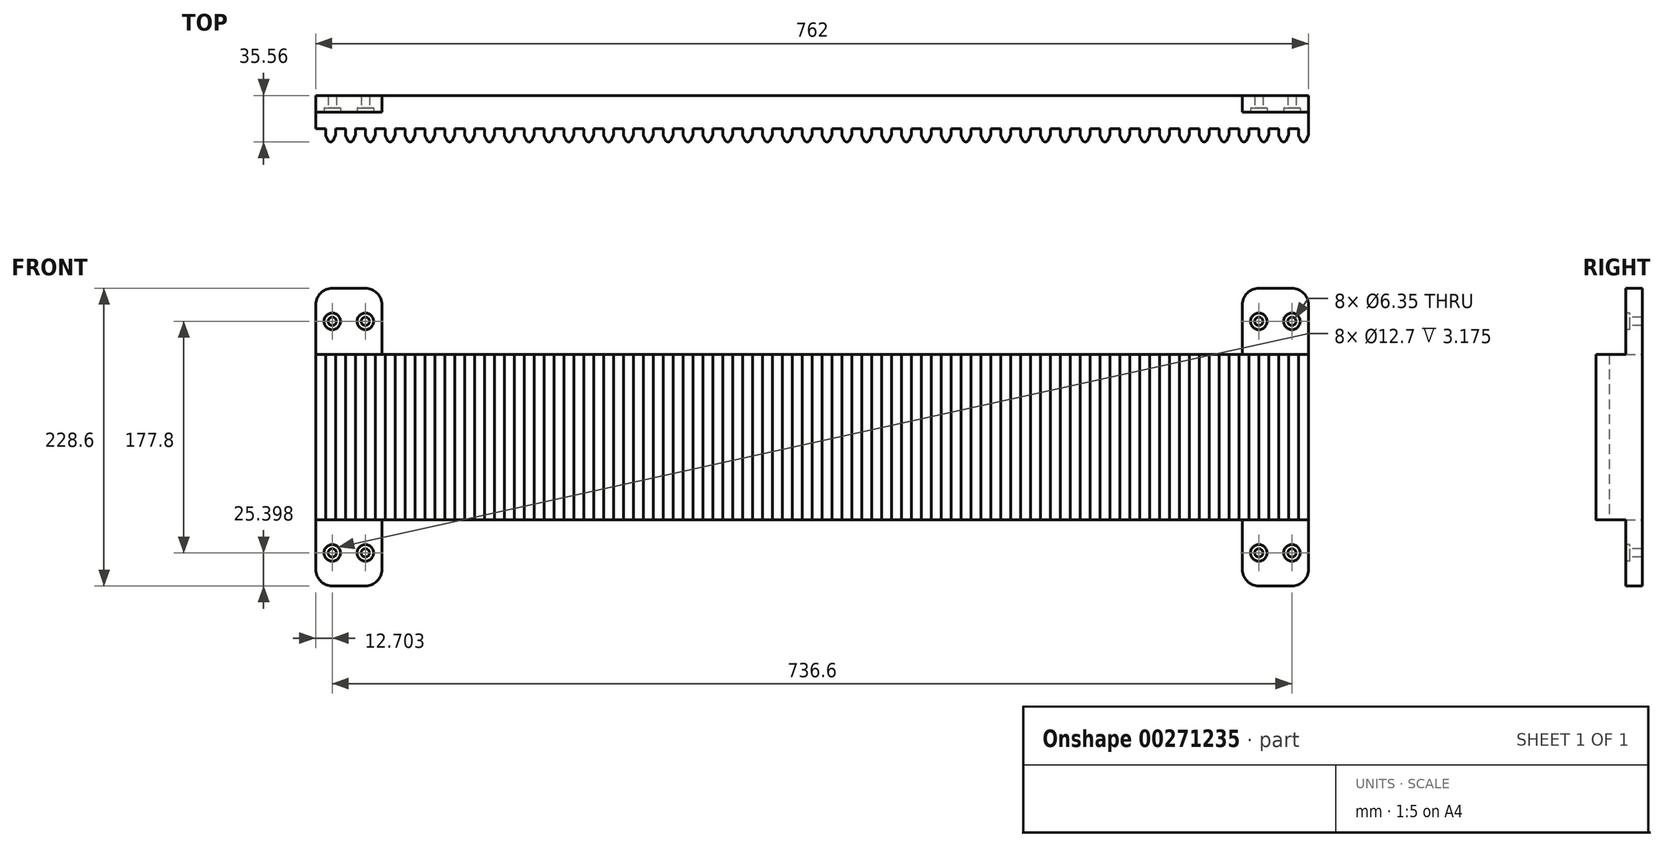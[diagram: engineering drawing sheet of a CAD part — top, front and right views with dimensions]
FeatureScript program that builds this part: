
annotation { "Feature Type Name" : "Feature", "Feature Type Description" : "" }
export const myFeature = defineFeature(function(context is Context, id is Id, definition is map)
    precondition{}
    {
        {
            var Q0;
            Q0=qCreatedBy(makeId("Front.planeOp"),FACE);
            var sketch = newSketch(context, id + "F0", { "sketchPlane" : qUnion([Q0])});
            skLineSegment(sketch, "E0", {"start": v(-383.67, -271.66) * mm, "end": v(378.33, -271.66) * mm});
            skLineSegment(sketch, "E1", {"start": v(378.33, -271.66) * mm, "end": v(378.33, -144.66) * mm});
            skLineSegment(sketch, "E2", {"start": v(378.33, -144.66) * mm, "end": v(-383.67, -144.66) * mm});
            skLineSegment(sketch, "E3", {"start": v(-383.67, -144.66) * mm, "end": v(-383.67, -271.66) * mm});
            skSolve(sketch);
        }
        {
            var Q0;
            Q0=makeQuery(id+"F0.imprint","IMPRINT",FACE,{"disambiguationData":[TD([[makeQuery(id+"F0.imprint","IMPRINT",EDGE,{"derivedFrom":sQuery(id+"F0.wireOp",EDGE,"E0")}),1.0]])]});
            extrude(context, id + "F1", {"entities" : qUnion([Q0]), "depth" : 25.4 * mm});
        }
        {
            var Q0;
            Q0=makeQuery(id+"F1.opExtrude","SWEPT_FACE",FACE,{"disambiguationData":[OSD([sQuery(id+"F0.wireOp",EDGE,"E0")])]});
            var sketch = newSketch(context, id + "F2", { "sketchPlane" : qUnion([Q0])});
            skLineSegment(sketch, "E4", {"start": v(-383.67, 25.4) * mm, "end": v(-376.05, 25.4) * mm});
            skLineSegment(sketch, "E5", {"start": v(-376.05, 25.4) * mm, "end": v(-376.05, 30.48) * mm});
            skLineSegment(sketch, "E6", {"start": v(-375.9, 30.8) * mm, "end": v(-374.1, 34.64) * mm});
            skLineSegment(sketch, "E7", {"start": v(-372.67, 35.56) * mm, "end": v(-371.8, 35.56) * mm});
            skLineSegment(sketch, "E8", {"start": v(-370.37, 34.64) * mm, "end": v(-368.58, 30.8) * mm});
            skLineSegment(sketch, "E9", {"start": v(-368.43, 30.13) * mm, "end": v(-368.43, 25.4) * mm});
            skLineSegment(sketch, "E10", {"start": v(-376.05, 30.13) * mm, "end": v(-376.05, 25.4) * mm});
            skPoint(sketch, "E11.visualSharp", {"position": v(-376.05, 30.48) * mm});
            skArc(sketch, "E11.filletArc", {"start": v(-375.9, 30.8) * mm, "mid": v(-376, 30.47) * mm, "end": v(-376.05, 30.13) * mm});
            skPoint(sketch, "E12.visualSharp", {"position": v(-368.43, 30.48) * mm});
            skArc(sketch, "E12.filletArc", {"start": v(-368.43, 30.13) * mm, "mid": v(-368.46, 30.47) * mm, "end": v(-368.58, 30.8) * mm});
            skPoint(sketch, "E13.visualSharp", {"position": v(-373.68, 35.56) * mm});
            skArc(sketch, "E13.filletArc", {"start": v(-372.67, 35.56) * mm, "mid": v(-373.52, 35.31) * mm, "end": v(-374.1, 34.64) * mm});
            skPoint(sketch, "E14.visualSharp", {"position": v(-370.8, 35.56) * mm});
            skArc(sketch, "E14.filletArc", {"start": v(-370.37, 34.64) * mm, "mid": v(-370.95, 35.31) * mm, "end": v(-371.8, 35.56) * mm});
            skLineSegment(sketch, "E15.1.0.0", {"start": v(-368.43, 25.4) * mm, "end": v(-360.8, 25.4) * mm});
            skLineSegment(sketch, "E15.1.0.1", {"start": v(-360.8, 30.13) * mm, "end": v(-360.8, 25.4) * mm});
            skArc(sketch, "E15.1.0.2", {"start": v(-360.66, 30.8) * mm, "mid": v(-360.77, 30.47) * mm, "end": v(-360.8, 30.13) * mm});
            skLineSegment(sketch, "E15.1.0.3", {"start": v(-360.66, 30.8) * mm, "end": v(-358.87, 34.64) * mm});
            skArc(sketch, "E15.1.0.4", {"start": v(-357.43, 35.56) * mm, "mid": v(-358.28, 35.31) * mm, "end": v(-358.87, 34.64) * mm});
            skLineSegment(sketch, "E15.1.0.5", {"start": v(-357.43, 35.56) * mm, "end": v(-356.57, 35.56) * mm});
            skArc(sketch, "E15.1.0.6", {"start": v(-355.13, 34.64) * mm, "mid": v(-355.71, 35.31) * mm, "end": v(-356.57, 35.56) * mm});
            skLineSegment(sketch, "E15.1.0.7", {"start": v(-355.13, 34.64) * mm, "end": v(-353.34, 30.8) * mm});
            skArc(sketch, "E15.1.0.8", {"start": v(-353.19, 30.13) * mm, "mid": v(-353.22, 30.47) * mm, "end": v(-353.34, 30.8) * mm});
            skLineSegment(sketch, "E15.1.0.9", {"start": v(-353.19, 30.13) * mm, "end": v(-353.19, 25.4) * mm});
            skLineSegment(sketch, "E15.2.0.0", {"start": v(-353.19, 25.4) * mm, "end": v(-345.57, 25.4) * mm});
            skLineSegment(sketch, "E15.2.0.1", {"start": v(-345.57, 30.13) * mm, "end": v(-345.57, 25.4) * mm});
            skArc(sketch, "E15.2.0.2", {"start": v(-345.42, 30.8) * mm, "mid": v(-345.53, 30.47) * mm, "end": v(-345.57, 30.13) * mm});
            skLineSegment(sketch, "E15.2.0.3", {"start": v(-345.42, 30.8) * mm, "end": v(-343.63, 34.64) * mm});
            skArc(sketch, "E15.2.0.4", {"start": v(-342.19, 35.56) * mm, "mid": v(-343.04, 35.31) * mm, "end": v(-343.63, 34.64) * mm});
            skLineSegment(sketch, "E15.2.0.5", {"start": v(-342.19, 35.56) * mm, "end": v(-341.33, 35.56) * mm});
            skArc(sketch, "E15.2.0.6", {"start": v(-339.89, 34.64) * mm, "mid": v(-340.47, 35.31) * mm, "end": v(-341.33, 35.56) * mm});
            skLineSegment(sketch, "E15.2.0.7", {"start": v(-339.89, 34.64) * mm, "end": v(-338.1, 30.8) * mm});
            skArc(sketch, "E15.2.0.8", {"start": v(-337.95, 30.13) * mm, "mid": v(-337.98, 30.47) * mm, "end": v(-338.1, 30.8) * mm});
            skLineSegment(sketch, "E15.2.0.9", {"start": v(-337.95, 30.13) * mm, "end": v(-337.95, 25.4) * mm});
            skLineSegment(sketch, "E15.3.0.0", {"start": v(-337.95, 25.4) * mm, "end": v(-330.33, 25.4) * mm});
            skLineSegment(sketch, "E15.3.0.1", {"start": v(-330.33, 30.13) * mm, "end": v(-330.33, 25.4) * mm});
            skArc(sketch, "E15.3.0.2", {"start": v(-330.18, 30.8) * mm, "mid": v(-330.29, 30.47) * mm, "end": v(-330.33, 30.13) * mm});
            skLineSegment(sketch, "E15.3.0.3", {"start": v(-330.18, 30.8) * mm, "end": v(-328.39, 34.64) * mm});
            skArc(sketch, "E15.3.0.4", {"start": v(-326.95, 35.56) * mm, "mid": v(-327.8, 35.31) * mm, "end": v(-328.39, 34.64) * mm});
            skLineSegment(sketch, "E15.3.0.5", {"start": v(-326.95, 35.56) * mm, "end": v(-326.09, 35.56) * mm});
            skArc(sketch, "E15.3.0.6", {"start": v(-324.65, 34.64) * mm, "mid": v(-325.23, 35.31) * mm, "end": v(-326.09, 35.56) * mm});
            skLineSegment(sketch, "E15.3.0.7", {"start": v(-324.65, 34.64) * mm, "end": v(-322.86, 30.8) * mm});
            skArc(sketch, "E15.3.0.8", {"start": v(-322.7, 30.13) * mm, "mid": v(-322.74, 30.47) * mm, "end": v(-322.86, 30.8) * mm});
            skLineSegment(sketch, "E15.3.0.9", {"start": v(-322.7, 30.13) * mm, "end": v(-322.7, 25.4) * mm});
            skLineSegment(sketch, "E15.4.0.0", {"start": v(-322.7, 25.4) * mm, "end": v(-315.09, 25.4) * mm});
            skLineSegment(sketch, "E15.4.0.1", {"start": v(-315.09, 30.13) * mm, "end": v(-315.09, 25.4) * mm});
            skArc(sketch, "E15.4.0.2", {"start": v(-314.94, 30.8) * mm, "mid": v(-315.05, 30.47) * mm, "end": v(-315.09, 30.13) * mm});
            skLineSegment(sketch, "E15.4.0.3", {"start": v(-314.94, 30.8) * mm, "end": v(-313.15, 34.64) * mm});
            skArc(sketch, "E15.4.0.4", {"start": v(-311.7, 35.56) * mm, "mid": v(-312.56, 35.31) * mm, "end": v(-313.15, 34.64) * mm});
            skLineSegment(sketch, "E15.4.0.5", {"start": v(-311.7, 35.56) * mm, "end": v(-310.85, 35.56) * mm});
            skArc(sketch, "E15.4.0.6", {"start": v(-309.4, 34.64) * mm, "mid": v(-310, 35.31) * mm, "end": v(-310.85, 35.56) * mm});
            skLineSegment(sketch, "E15.4.0.7", {"start": v(-309.4, 34.64) * mm, "end": v(-307.62, 30.8) * mm});
            skArc(sketch, "E15.4.0.8", {"start": v(-307.47, 30.13) * mm, "mid": v(-307.5, 30.47) * mm, "end": v(-307.62, 30.8) * mm});
            skLineSegment(sketch, "E15.4.0.9", {"start": v(-307.47, 30.13) * mm, "end": v(-307.47, 25.4) * mm});
            skLineSegment(sketch, "E15.5.0.0", {"start": v(-307.47, 25.4) * mm, "end": v(-299.85, 25.4) * mm});
            skLineSegment(sketch, "E15.5.0.1", {"start": v(-299.85, 30.13) * mm, "end": v(-299.85, 25.4) * mm});
            skArc(sketch, "E15.5.0.2", {"start": v(-299.7, 30.8) * mm, "mid": v(-299.8, 30.47) * mm, "end": v(-299.85, 30.13) * mm});
            skLineSegment(sketch, "E15.5.0.3", {"start": v(-299.7, 30.8) * mm, "end": v(-297.9, 34.64) * mm});
            skArc(sketch, "E15.5.0.4", {"start": v(-296.47, 35.56) * mm, "mid": v(-297.32, 35.31) * mm, "end": v(-297.9, 34.64) * mm});
            skLineSegment(sketch, "E15.5.0.5", {"start": v(-296.47, 35.56) * mm, "end": v(-295.6, 35.56) * mm});
            skArc(sketch, "E15.5.0.6", {"start": v(-294.17, 34.64) * mm, "mid": v(-294.75, 35.31) * mm, "end": v(-295.6, 35.56) * mm});
            skLineSegment(sketch, "E15.5.0.7", {"start": v(-294.17, 34.64) * mm, "end": v(-292.38, 30.8) * mm});
            skArc(sketch, "E15.5.0.8", {"start": v(-292.23, 30.13) * mm, "mid": v(-292.26, 30.47) * mm, "end": v(-292.38, 30.8) * mm});
            skLineSegment(sketch, "E15.5.0.9", {"start": v(-292.23, 30.13) * mm, "end": v(-292.23, 25.4) * mm});
            skLineSegment(sketch, "E15.6.0.0", {"start": v(-292.23, 25.4) * mm, "end": v(-284.6, 25.4) * mm});
            skLineSegment(sketch, "E15.6.0.1", {"start": v(-284.6, 30.13) * mm, "end": v(-284.6, 25.4) * mm});
            skArc(sketch, "E15.6.0.2", {"start": v(-284.46, 30.8) * mm, "mid": v(-284.57, 30.47) * mm, "end": v(-284.6, 30.13) * mm});
            skLineSegment(sketch, "E15.6.0.3", {"start": v(-284.46, 30.8) * mm, "end": v(-282.67, 34.64) * mm});
            skArc(sketch, "E15.6.0.4", {"start": v(-281.23, 35.56) * mm, "mid": v(-282.08, 35.31) * mm, "end": v(-282.67, 34.64) * mm});
            skLineSegment(sketch, "E15.6.0.5", {"start": v(-281.23, 35.56) * mm, "end": v(-280.37, 35.56) * mm});
            skArc(sketch, "E15.6.0.6", {"start": v(-278.93, 34.64) * mm, "mid": v(-279.51, 35.31) * mm, "end": v(-280.37, 35.56) * mm});
            skLineSegment(sketch, "E15.6.0.7", {"start": v(-278.93, 34.64) * mm, "end": v(-277.14, 30.8) * mm});
            skArc(sketch, "E15.6.0.8", {"start": v(-276.99, 30.13) * mm, "mid": v(-277.02, 30.47) * mm, "end": v(-277.14, 30.8) * mm});
            skLineSegment(sketch, "E15.6.0.9", {"start": v(-276.99, 30.13) * mm, "end": v(-276.99, 25.4) * mm});
            skLineSegment(sketch, "E15.7.0.0", {"start": v(-276.99, 25.4) * mm, "end": v(-269.37, 25.4) * mm});
            skLineSegment(sketch, "E15.7.0.1", {"start": v(-269.37, 30.13) * mm, "end": v(-269.37, 25.4) * mm});
            skArc(sketch, "E15.7.0.2", {"start": v(-269.22, 30.8) * mm, "mid": v(-269.33, 30.47) * mm, "end": v(-269.37, 30.13) * mm});
            skLineSegment(sketch, "E15.7.0.3", {"start": v(-269.22, 30.8) * mm, "end": v(-267.43, 34.64) * mm});
            skArc(sketch, "E15.7.0.4", {"start": v(-265.99, 35.56) * mm, "mid": v(-266.84, 35.31) * mm, "end": v(-267.43, 34.64) * mm});
            skLineSegment(sketch, "E15.7.0.5", {"start": v(-265.99, 35.56) * mm, "end": v(-265.13, 35.56) * mm});
            skArc(sketch, "E15.7.0.6", {"start": v(-263.69, 34.64) * mm, "mid": v(-264.27, 35.31) * mm, "end": v(-265.13, 35.56) * mm});
            skLineSegment(sketch, "E15.7.0.7", {"start": v(-263.69, 34.64) * mm, "end": v(-261.9, 30.8) * mm});
            skArc(sketch, "E15.7.0.8", {"start": v(-261.75, 30.13) * mm, "mid": v(-261.78, 30.47) * mm, "end": v(-261.9, 30.8) * mm});
            skLineSegment(sketch, "E15.7.0.9", {"start": v(-261.75, 30.13) * mm, "end": v(-261.75, 25.4) * mm});
            skLineSegment(sketch, "E15.8.0.0", {"start": v(-261.75, 25.4) * mm, "end": v(-254.13, 25.4) * mm});
            skLineSegment(sketch, "E15.8.0.1", {"start": v(-254.13, 30.13) * mm, "end": v(-254.13, 25.4) * mm});
            skArc(sketch, "E15.8.0.2", {"start": v(-253.98, 30.8) * mm, "mid": v(-254.09, 30.47) * mm, "end": v(-254.13, 30.13) * mm});
            skLineSegment(sketch, "E15.8.0.3", {"start": v(-253.98, 30.8) * mm, "end": v(-252.19, 34.64) * mm});
            skArc(sketch, "E15.8.0.4", {"start": v(-250.75, 35.56) * mm, "mid": v(-251.6, 35.31) * mm, "end": v(-252.19, 34.64) * mm});
            skLineSegment(sketch, "E15.8.0.5", {"start": v(-250.75, 35.56) * mm, "end": v(-249.89, 35.56) * mm});
            skArc(sketch, "E15.8.0.6", {"start": v(-248.45, 34.64) * mm, "mid": v(-249.03, 35.31) * mm, "end": v(-249.89, 35.56) * mm});
            skLineSegment(sketch, "E15.8.0.7", {"start": v(-248.45, 34.64) * mm, "end": v(-246.66, 30.8) * mm});
            skArc(sketch, "E15.8.0.8", {"start": v(-246.5, 30.13) * mm, "mid": v(-246.54, 30.47) * mm, "end": v(-246.66, 30.8) * mm});
            skLineSegment(sketch, "E15.8.0.9", {"start": v(-246.5, 30.13) * mm, "end": v(-246.5, 25.4) * mm});
            skLineSegment(sketch, "E15.9.0.0", {"start": v(-246.5, 25.4) * mm, "end": v(-238.89, 25.4) * mm});
            skLineSegment(sketch, "E15.9.0.1", {"start": v(-238.89, 30.13) * mm, "end": v(-238.89, 25.4) * mm});
            skArc(sketch, "E15.9.0.2", {"start": v(-238.74, 30.8) * mm, "mid": v(-238.85, 30.47) * mm, "end": v(-238.89, 30.13) * mm});
            skLineSegment(sketch, "E15.9.0.3", {"start": v(-238.74, 30.8) * mm, "end": v(-236.95, 34.64) * mm});
            skArc(sketch, "E15.9.0.4", {"start": v(-235.5, 35.56) * mm, "mid": v(-236.36, 35.31) * mm, "end": v(-236.95, 34.64) * mm});
            skLineSegment(sketch, "E15.9.0.5", {"start": v(-235.5, 35.56) * mm, "end": v(-234.65, 35.56) * mm});
            skArc(sketch, "E15.9.0.6", {"start": v(-233.2, 34.64) * mm, "mid": v(-233.8, 35.31) * mm, "end": v(-234.65, 35.56) * mm});
            skLineSegment(sketch, "E15.9.0.7", {"start": v(-233.2, 34.64) * mm, "end": v(-231.42, 30.8) * mm});
            skArc(sketch, "E15.9.0.8", {"start": v(-231.27, 30.13) * mm, "mid": v(-231.3, 30.47) * mm, "end": v(-231.42, 30.8) * mm});
            skLineSegment(sketch, "E15.9.0.9", {"start": v(-231.27, 30.13) * mm, "end": v(-231.27, 25.4) * mm});
            skLineSegment(sketch, "E15.10.0.0", {"start": v(-231.27, 25.4) * mm, "end": v(-223.65, 25.4) * mm});
            skLineSegment(sketch, "E15.10.0.1", {"start": v(-223.65, 30.13) * mm, "end": v(-223.65, 25.4) * mm});
            skArc(sketch, "E15.10.0.2", {"start": v(-223.5, 30.8) * mm, "mid": v(-223.6, 30.47) * mm, "end": v(-223.65, 30.13) * mm});
            skLineSegment(sketch, "E15.10.0.3", {"start": v(-223.5, 30.8) * mm, "end": v(-221.7, 34.64) * mm});
            skArc(sketch, "E15.10.0.4", {"start": v(-220.27, 35.56) * mm, "mid": v(-221.12, 35.31) * mm, "end": v(-221.7, 34.64) * mm});
            skLineSegment(sketch, "E15.10.0.5", {"start": v(-220.27, 35.56) * mm, "end": v(-219.4, 35.56) * mm});
            skArc(sketch, "E15.10.0.6", {"start": v(-217.97, 34.64) * mm, "mid": v(-218.55, 35.31) * mm, "end": v(-219.4, 35.56) * mm});
            skLineSegment(sketch, "E15.10.0.7", {"start": v(-217.97, 34.64) * mm, "end": v(-216.18, 30.8) * mm});
            skArc(sketch, "E15.10.0.8", {"start": v(-216.03, 30.13) * mm, "mid": v(-216.06, 30.47) * mm, "end": v(-216.18, 30.8) * mm});
            skLineSegment(sketch, "E15.10.0.9", {"start": v(-216.03, 30.13) * mm, "end": v(-216.03, 25.4) * mm});
            skLineSegment(sketch, "E15.11.0.0", {"start": v(-216.03, 25.4) * mm, "end": v(-208.4, 25.4) * mm});
            skLineSegment(sketch, "E15.11.0.1", {"start": v(-208.4, 30.13) * mm, "end": v(-208.4, 25.4) * mm});
            skArc(sketch, "E15.11.0.2", {"start": v(-208.26, 30.8) * mm, "mid": v(-208.37, 30.47) * mm, "end": v(-208.4, 30.13) * mm});
            skLineSegment(sketch, "E15.11.0.3", {"start": v(-208.26, 30.8) * mm, "end": v(-206.47, 34.64) * mm});
            skArc(sketch, "E15.11.0.4", {"start": v(-205.03, 35.56) * mm, "mid": v(-205.88, 35.31) * mm, "end": v(-206.47, 34.64) * mm});
            skLineSegment(sketch, "E15.11.0.5", {"start": v(-205.03, 35.56) * mm, "end": v(-204.17, 35.56) * mm});
            skArc(sketch, "E15.11.0.6", {"start": v(-202.73, 34.64) * mm, "mid": v(-203.31, 35.31) * mm, "end": v(-204.17, 35.56) * mm});
            skLineSegment(sketch, "E15.11.0.7", {"start": v(-202.73, 34.64) * mm, "end": v(-200.94, 30.8) * mm});
            skArc(sketch, "E15.11.0.8", {"start": v(-200.79, 30.13) * mm, "mid": v(-200.82, 30.47) * mm, "end": v(-200.94, 30.8) * mm});
            skLineSegment(sketch, "E15.11.0.9", {"start": v(-200.79, 30.13) * mm, "end": v(-200.79, 25.4) * mm});
            skLineSegment(sketch, "E15.12.0.0", {"start": v(-200.79, 25.4) * mm, "end": v(-193.17, 25.4) * mm});
            skLineSegment(sketch, "E15.12.0.1", {"start": v(-193.17, 30.13) * mm, "end": v(-193.17, 25.4) * mm});
            skArc(sketch, "E15.12.0.2", {"start": v(-193.02, 30.8) * mm, "mid": v(-193.13, 30.47) * mm, "end": v(-193.17, 30.13) * mm});
            skLineSegment(sketch, "E15.12.0.3", {"start": v(-193.02, 30.8) * mm, "end": v(-191.23, 34.64) * mm});
            skArc(sketch, "E15.12.0.4", {"start": v(-189.79, 35.56) * mm, "mid": v(-190.64, 35.31) * mm, "end": v(-191.23, 34.64) * mm});
            skLineSegment(sketch, "E15.12.0.5", {"start": v(-189.79, 35.56) * mm, "end": v(-188.93, 35.56) * mm});
            skArc(sketch, "E15.12.0.6", {"start": v(-187.49, 34.64) * mm, "mid": v(-188.07, 35.31) * mm, "end": v(-188.93, 35.56) * mm});
            skLineSegment(sketch, "E15.12.0.7", {"start": v(-187.49, 34.64) * mm, "end": v(-185.7, 30.8) * mm});
            skArc(sketch, "E15.12.0.8", {"start": v(-185.55, 30.13) * mm, "mid": v(-185.58, 30.47) * mm, "end": v(-185.7, 30.8) * mm});
            skLineSegment(sketch, "E15.12.0.9", {"start": v(-185.55, 30.13) * mm, "end": v(-185.55, 25.4) * mm});
            skLineSegment(sketch, "E15.13.0.0", {"start": v(-185.55, 25.4) * mm, "end": v(-177.93, 25.4) * mm});
            skLineSegment(sketch, "E15.13.0.1", {"start": v(-177.93, 30.13) * mm, "end": v(-177.93, 25.4) * mm});
            skArc(sketch, "E15.13.0.2", {"start": v(-177.78, 30.8) * mm, "mid": v(-177.89, 30.47) * mm, "end": v(-177.93, 30.13) * mm});
            skLineSegment(sketch, "E15.13.0.3", {"start": v(-177.78, 30.8) * mm, "end": v(-175.99, 34.64) * mm});
            skArc(sketch, "E15.13.0.4", {"start": v(-174.55, 35.56) * mm, "mid": v(-175.4, 35.31) * mm, "end": v(-175.99, 34.64) * mm});
            skLineSegment(sketch, "E15.13.0.5", {"start": v(-174.55, 35.56) * mm, "end": v(-173.69, 35.56) * mm});
            skArc(sketch, "E15.13.0.6", {"start": v(-172.25, 34.64) * mm, "mid": v(-172.83, 35.31) * mm, "end": v(-173.69, 35.56) * mm});
            skLineSegment(sketch, "E15.13.0.7", {"start": v(-172.25, 34.64) * mm, "end": v(-170.46, 30.8) * mm});
            skArc(sketch, "E15.13.0.8", {"start": v(-170.3, 30.13) * mm, "mid": v(-170.34, 30.47) * mm, "end": v(-170.46, 30.8) * mm});
            skLineSegment(sketch, "E15.13.0.9", {"start": v(-170.3, 30.13) * mm, "end": v(-170.3, 25.4) * mm});
            skLineSegment(sketch, "E15.14.0.0", {"start": v(-170.3, 25.4) * mm, "end": v(-162.69, 25.4) * mm});
            skLineSegment(sketch, "E15.14.0.1", {"start": v(-162.69, 30.13) * mm, "end": v(-162.69, 25.4) * mm});
            skArc(sketch, "E15.14.0.2", {"start": v(-162.54, 30.8) * mm, "mid": v(-162.65, 30.47) * mm, "end": v(-162.69, 30.13) * mm});
            skLineSegment(sketch, "E15.14.0.3", {"start": v(-162.54, 30.8) * mm, "end": v(-160.75, 34.64) * mm});
            skArc(sketch, "E15.14.0.4", {"start": v(-159.3, 35.56) * mm, "mid": v(-160.16, 35.31) * mm, "end": v(-160.75, 34.64) * mm});
            skLineSegment(sketch, "E15.14.0.5", {"start": v(-159.3, 35.56) * mm, "end": v(-158.45, 35.56) * mm});
            skArc(sketch, "E15.14.0.6", {"start": v(-157, 34.64) * mm, "mid": v(-157.6, 35.31) * mm, "end": v(-158.45, 35.56) * mm});
            skLineSegment(sketch, "E15.14.0.7", {"start": v(-157, 34.64) * mm, "end": v(-155.22, 30.8) * mm});
            skArc(sketch, "E15.14.0.8", {"start": v(-155.07, 30.13) * mm, "mid": v(-155.1, 30.47) * mm, "end": v(-155.22, 30.8) * mm});
            skLineSegment(sketch, "E15.14.0.9", {"start": v(-155.07, 30.13) * mm, "end": v(-155.07, 25.4) * mm});
            skLineSegment(sketch, "E15.15.0.0", {"start": v(-155.07, 25.4) * mm, "end": v(-147.45, 25.4) * mm});
            skLineSegment(sketch, "E15.15.0.1", {"start": v(-147.45, 30.13) * mm, "end": v(-147.45, 25.4) * mm});
            skArc(sketch, "E15.15.0.2", {"start": v(-147.3, 30.8) * mm, "mid": v(-147.4, 30.47) * mm, "end": v(-147.45, 30.13) * mm});
            skLineSegment(sketch, "E15.15.0.3", {"start": v(-147.3, 30.8) * mm, "end": v(-145.5, 34.64) * mm});
            skArc(sketch, "E15.15.0.4", {"start": v(-144.07, 35.56) * mm, "mid": v(-144.92, 35.31) * mm, "end": v(-145.5, 34.64) * mm});
            skLineSegment(sketch, "E15.15.0.5", {"start": v(-144.07, 35.56) * mm, "end": v(-143.2, 35.56) * mm});
            skArc(sketch, "E15.15.0.6", {"start": v(-141.77, 34.64) * mm, "mid": v(-142.35, 35.31) * mm, "end": v(-143.2, 35.56) * mm});
            skLineSegment(sketch, "E15.15.0.7", {"start": v(-141.77, 34.64) * mm, "end": v(-139.98, 30.8) * mm});
            skArc(sketch, "E15.15.0.8", {"start": v(-139.83, 30.13) * mm, "mid": v(-139.86, 30.47) * mm, "end": v(-139.98, 30.8) * mm});
            skLineSegment(sketch, "E15.15.0.9", {"start": v(-139.83, 30.13) * mm, "end": v(-139.83, 25.4) * mm});
            skLineSegment(sketch, "E15.16.0.0", {"start": v(-139.83, 25.4) * mm, "end": v(-132.2, 25.4) * mm});
            skLineSegment(sketch, "E15.16.0.1", {"start": v(-132.2, 30.13) * mm, "end": v(-132.2, 25.4) * mm});
            skArc(sketch, "E15.16.0.2", {"start": v(-132.06, 30.8) * mm, "mid": v(-132.17, 30.47) * mm, "end": v(-132.2, 30.13) * mm});
            skLineSegment(sketch, "E15.16.0.3", {"start": v(-132.06, 30.8) * mm, "end": v(-130.27, 34.64) * mm});
            skArc(sketch, "E15.16.0.4", {"start": v(-128.83, 35.56) * mm, "mid": v(-129.68, 35.31) * mm, "end": v(-130.27, 34.64) * mm});
            skLineSegment(sketch, "E15.16.0.5", {"start": v(-128.83, 35.56) * mm, "end": v(-127.97, 35.56) * mm});
            skArc(sketch, "E15.16.0.6", {"start": v(-126.53, 34.64) * mm, "mid": v(-127.11, 35.31) * mm, "end": v(-127.97, 35.56) * mm});
            skLineSegment(sketch, "E15.16.0.7", {"start": v(-126.53, 34.64) * mm, "end": v(-124.74, 30.8) * mm});
            skArc(sketch, "E15.16.0.8", {"start": v(-124.59, 30.13) * mm, "mid": v(-124.62, 30.47) * mm, "end": v(-124.74, 30.8) * mm});
            skLineSegment(sketch, "E15.16.0.9", {"start": v(-124.59, 30.13) * mm, "end": v(-124.59, 25.4) * mm});
            skLineSegment(sketch, "E15.17.0.0", {"start": v(-124.59, 25.4) * mm, "end": v(-116.97, 25.4) * mm});
            skLineSegment(sketch, "E15.17.0.1", {"start": v(-116.97, 30.13) * mm, "end": v(-116.97, 25.4) * mm});
            skArc(sketch, "E15.17.0.2", {"start": v(-116.82, 30.8) * mm, "mid": v(-116.93, 30.47) * mm, "end": v(-116.97, 30.13) * mm});
            skLineSegment(sketch, "E15.17.0.3", {"start": v(-116.82, 30.8) * mm, "end": v(-115.03, 34.64) * mm});
            skArc(sketch, "E15.17.0.4", {"start": v(-113.59, 35.56) * mm, "mid": v(-114.44, 35.31) * mm, "end": v(-115.03, 34.64) * mm});
            skLineSegment(sketch, "E15.17.0.5", {"start": v(-113.59, 35.56) * mm, "end": v(-112.73, 35.56) * mm});
            skArc(sketch, "E15.17.0.6", {"start": v(-111.29, 34.64) * mm, "mid": v(-111.87, 35.31) * mm, "end": v(-112.73, 35.56) * mm});
            skLineSegment(sketch, "E15.17.0.7", {"start": v(-111.29, 34.64) * mm, "end": v(-109.5, 30.8) * mm});
            skArc(sketch, "E15.17.0.8", {"start": v(-109.35, 30.13) * mm, "mid": v(-109.38, 30.47) * mm, "end": v(-109.5, 30.8) * mm});
            skLineSegment(sketch, "E15.17.0.9", {"start": v(-109.35, 30.13) * mm, "end": v(-109.35, 25.4) * mm});
            skLineSegment(sketch, "E15.18.0.0", {"start": v(-109.35, 25.4) * mm, "end": v(-101.73, 25.4) * mm});
            skLineSegment(sketch, "E15.18.0.1", {"start": v(-101.73, 30.13) * mm, "end": v(-101.73, 25.4) * mm});
            skArc(sketch, "E15.18.0.2", {"start": v(-101.58, 30.8) * mm, "mid": v(-101.69, 30.47) * mm, "end": v(-101.73, 30.13) * mm});
            skLineSegment(sketch, "E15.18.0.3", {"start": v(-101.58, 30.8) * mm, "end": v(-99.79, 34.64) * mm});
            skArc(sketch, "E15.18.0.4", {"start": v(-98.35, 35.56) * mm, "mid": v(-99.2, 35.31) * mm, "end": v(-99.79, 34.64) * mm});
            skLineSegment(sketch, "E15.18.0.5", {"start": v(-98.35, 35.56) * mm, "end": v(-97.49, 35.56) * mm});
            skArc(sketch, "E15.18.0.6", {"start": v(-96.05, 34.64) * mm, "mid": v(-96.63, 35.31) * mm, "end": v(-97.49, 35.56) * mm});
            skLineSegment(sketch, "E15.18.0.7", {"start": v(-96.05, 34.64) * mm, "end": v(-94.26, 30.8) * mm});
            skArc(sketch, "E15.18.0.8", {"start": v(-94.1, 30.13) * mm, "mid": v(-94.14, 30.47) * mm, "end": v(-94.26, 30.8) * mm});
            skLineSegment(sketch, "E15.18.0.9", {"start": v(-94.1, 30.13) * mm, "end": v(-94.1, 25.4) * mm});
            skLineSegment(sketch, "E15.19.0.0", {"start": v(-94.1, 25.4) * mm, "end": v(-86.49, 25.4) * mm});
            skLineSegment(sketch, "E15.19.0.1", {"start": v(-86.49, 30.13) * mm, "end": v(-86.49, 25.4) * mm});
            skArc(sketch, "E15.19.0.2", {"start": v(-86.34, 30.8) * mm, "mid": v(-86.45, 30.47) * mm, "end": v(-86.49, 30.13) * mm});
            skLineSegment(sketch, "E15.19.0.3", {"start": v(-86.34, 30.8) * mm, "end": v(-84.55, 34.64) * mm});
            skArc(sketch, "E15.19.0.4", {"start": v(-83.1, 35.56) * mm, "mid": v(-83.96, 35.31) * mm, "end": v(-84.55, 34.64) * mm});
            skLineSegment(sketch, "E15.19.0.5", {"start": v(-83.1, 35.56) * mm, "end": v(-82.25, 35.56) * mm});
            skArc(sketch, "E15.19.0.6", {"start": v(-80.8, 34.64) * mm, "mid": v(-81.4, 35.31) * mm, "end": v(-82.25, 35.56) * mm});
            skLineSegment(sketch, "E15.19.0.7", {"start": v(-80.8, 34.64) * mm, "end": v(-79.02, 30.8) * mm});
            skArc(sketch, "E15.19.0.8", {"start": v(-78.87, 30.13) * mm, "mid": v(-78.9, 30.47) * mm, "end": v(-79.02, 30.8) * mm});
            skLineSegment(sketch, "E15.19.0.9", {"start": v(-78.87, 30.13) * mm, "end": v(-78.87, 25.4) * mm});
            skLineSegment(sketch, "E15.20.0.0", {"start": v(-78.87, 25.4) * mm, "end": v(-71.25, 25.4) * mm});
            skLineSegment(sketch, "E15.20.0.1", {"start": v(-71.25, 30.13) * mm, "end": v(-71.25, 25.4) * mm});
            skArc(sketch, "E15.20.0.2", {"start": v(-71.1, 30.8) * mm, "mid": v(-71.2, 30.47) * mm, "end": v(-71.25, 30.13) * mm});
            skLineSegment(sketch, "E15.20.0.3", {"start": v(-71.1, 30.8) * mm, "end": v(-69.3, 34.64) * mm});
            skArc(sketch, "E15.20.0.4", {"start": v(-67.87, 35.56) * mm, "mid": v(-68.72, 35.31) * mm, "end": v(-69.3, 34.64) * mm});
            skLineSegment(sketch, "E15.20.0.5", {"start": v(-67.87, 35.56) * mm, "end": v(-67, 35.56) * mm});
            skArc(sketch, "E15.20.0.6", {"start": v(-65.57, 34.64) * mm, "mid": v(-66.15, 35.31) * mm, "end": v(-67, 35.56) * mm});
            skLineSegment(sketch, "E15.20.0.7", {"start": v(-65.57, 34.64) * mm, "end": v(-63.78, 30.8) * mm});
            skArc(sketch, "E15.20.0.8", {"start": v(-63.63, 30.13) * mm, "mid": v(-63.66, 30.47) * mm, "end": v(-63.78, 30.8) * mm});
            skLineSegment(sketch, "E15.20.0.9", {"start": v(-63.63, 30.13) * mm, "end": v(-63.63, 25.4) * mm});
            skLineSegment(sketch, "E15.21.0.0", {"start": v(-63.63, 25.4) * mm, "end": v(-56, 25.4) * mm});
            skLineSegment(sketch, "E15.21.0.1", {"start": v(-56, 30.13) * mm, "end": v(-56, 25.4) * mm});
            skArc(sketch, "E15.21.0.2", {"start": v(-55.86, 30.8) * mm, "mid": v(-55.97, 30.47) * mm, "end": v(-56, 30.13) * mm});
            skLineSegment(sketch, "E15.21.0.3", {"start": v(-55.86, 30.8) * mm, "end": v(-54.07, 34.64) * mm});
            skArc(sketch, "E15.21.0.4", {"start": v(-52.63, 35.56) * mm, "mid": v(-53.48, 35.31) * mm, "end": v(-54.07, 34.64) * mm});
            skLineSegment(sketch, "E15.21.0.5", {"start": v(-52.63, 35.56) * mm, "end": v(-51.77, 35.56) * mm});
            skArc(sketch, "E15.21.0.6", {"start": v(-50.33, 34.64) * mm, "mid": v(-50.91, 35.31) * mm, "end": v(-51.77, 35.56) * mm});
            skLineSegment(sketch, "E15.21.0.7", {"start": v(-50.33, 34.64) * mm, "end": v(-48.54, 30.8) * mm});
            skArc(sketch, "E15.21.0.8", {"start": v(-48.39, 30.13) * mm, "mid": v(-48.42, 30.47) * mm, "end": v(-48.54, 30.8) * mm});
            skLineSegment(sketch, "E15.21.0.9", {"start": v(-48.39, 30.13) * mm, "end": v(-48.39, 25.4) * mm});
            skLineSegment(sketch, "E15.22.0.0", {"start": v(-48.39, 25.4) * mm, "end": v(-40.77, 25.4) * mm});
            skLineSegment(sketch, "E15.22.0.1", {"start": v(-40.77, 30.13) * mm, "end": v(-40.77, 25.4) * mm});
            skArc(sketch, "E15.22.0.2", {"start": v(-40.62, 30.8) * mm, "mid": v(-40.73, 30.47) * mm, "end": v(-40.77, 30.13) * mm});
            skLineSegment(sketch, "E15.22.0.3", {"start": v(-40.62, 30.8) * mm, "end": v(-38.83, 34.64) * mm});
            skArc(sketch, "E15.22.0.4", {"start": v(-37.39, 35.56) * mm, "mid": v(-38.24, 35.31) * mm, "end": v(-38.83, 34.64) * mm});
            skLineSegment(sketch, "E15.22.0.5", {"start": v(-37.39, 35.56) * mm, "end": v(-36.53, 35.56) * mm});
            skArc(sketch, "E15.22.0.6", {"start": v(-35.09, 34.64) * mm, "mid": v(-35.67, 35.31) * mm, "end": v(-36.53, 35.56) * mm});
            skLineSegment(sketch, "E15.22.0.7", {"start": v(-35.09, 34.64) * mm, "end": v(-33.3, 30.8) * mm});
            skArc(sketch, "E15.22.0.8", {"start": v(-33.15, 30.13) * mm, "mid": v(-33.18, 30.47) * mm, "end": v(-33.3, 30.8) * mm});
            skLineSegment(sketch, "E15.22.0.9", {"start": v(-33.15, 30.13) * mm, "end": v(-33.15, 25.4) * mm});
            skLineSegment(sketch, "E15.23.0.0", {"start": v(-33.15, 25.4) * mm, "end": v(-25.53, 25.4) * mm});
            skLineSegment(sketch, "E15.23.0.1", {"start": v(-25.53, 30.13) * mm, "end": v(-25.53, 25.4) * mm});
            skArc(sketch, "E15.23.0.2", {"start": v(-25.38, 30.8) * mm, "mid": v(-25.49, 30.47) * mm, "end": v(-25.53, 30.13) * mm});
            skLineSegment(sketch, "E15.23.0.3", {"start": v(-25.38, 30.8) * mm, "end": v(-23.59, 34.64) * mm});
            skArc(sketch, "E15.23.0.4", {"start": v(-22.15, 35.56) * mm, "mid": v(-23, 35.31) * mm, "end": v(-23.59, 34.64) * mm});
            skLineSegment(sketch, "E15.23.0.5", {"start": v(-22.15, 35.56) * mm, "end": v(-21.29, 35.56) * mm});
            skArc(sketch, "E15.23.0.6", {"start": v(-19.85, 34.64) * mm, "mid": v(-20.43, 35.31) * mm, "end": v(-21.29, 35.56) * mm});
            skLineSegment(sketch, "E15.23.0.7", {"start": v(-19.85, 34.64) * mm, "end": v(-18.06, 30.8) * mm});
            skArc(sketch, "E15.23.0.8", {"start": v(-17.9, 30.13) * mm, "mid": v(-17.94, 30.47) * mm, "end": v(-18.06, 30.8) * mm});
            skLineSegment(sketch, "E15.23.0.9", {"start": v(-17.9, 30.13) * mm, "end": v(-17.9, 25.4) * mm});
            skLineSegment(sketch, "E15.24.0.0", {"start": v(-17.9, 25.4) * mm, "end": v(-10.29, 25.4) * mm});
            skLineSegment(sketch, "E15.24.0.1", {"start": v(-10.29, 30.13) * mm, "end": v(-10.29, 25.4) * mm});
            skArc(sketch, "E15.24.0.2", {"start": v(-10.14, 30.8) * mm, "mid": v(-10.25, 30.47) * mm, "end": v(-10.29, 30.13) * mm});
            skLineSegment(sketch, "E15.24.0.3", {"start": v(-10.14, 30.8) * mm, "end": v(-8.35, 34.64) * mm});
            skArc(sketch, "E15.24.0.4", {"start": v(-6.9, 35.56) * mm, "mid": v(-7.76, 35.31) * mm, "end": v(-8.35, 34.64) * mm});
            skLineSegment(sketch, "E15.24.0.5", {"start": v(-6.9, 35.56) * mm, "end": v(-6.05, 35.56) * mm});
            skArc(sketch, "E15.24.0.6", {"start": v(-4.6, 34.64) * mm, "mid": v(-5.2, 35.31) * mm, "end": v(-6.05, 35.56) * mm});
            skLineSegment(sketch, "E15.24.0.7", {"start": v(-4.6, 34.64) * mm, "end": v(-2.82, 30.8) * mm});
            skArc(sketch, "E15.24.0.8", {"start": v(-2.67, 30.13) * mm, "mid": v(-2.7, 30.47) * mm, "end": v(-2.82, 30.8) * mm});
            skLineSegment(sketch, "E15.24.0.9", {"start": v(-2.67, 30.13) * mm, "end": v(-2.67, 25.4) * mm});
            skLineSegment(sketch, "E15.25.0.0", {"start": v(-2.67, 25.4) * mm, "end": v(4.95, 25.4) * mm});
            skLineSegment(sketch, "E15.25.0.1", {"start": v(4.95, 30.13) * mm, "end": v(4.95, 25.4) * mm});
            skArc(sketch, "E15.25.0.2", {"start": v(5.1, 30.8) * mm, "mid": v(5, 30.47) * mm, "end": v(4.95, 30.13) * mm});
            skLineSegment(sketch, "E15.25.0.3", {"start": v(5.1, 30.8) * mm, "end": v(6.9, 34.64) * mm});
            skArc(sketch, "E15.25.0.4", {"start": v(8.33, 35.56) * mm, "mid": v(7.48, 35.31) * mm, "end": v(6.9, 34.64) * mm});
            skLineSegment(sketch, "E15.25.0.5", {"start": v(8.33, 35.56) * mm, "end": v(9.2, 35.56) * mm});
            skArc(sketch, "E15.25.0.6", {"start": v(10.63, 34.64) * mm, "mid": v(10.05, 35.31) * mm, "end": v(9.2, 35.56) * mm});
            skLineSegment(sketch, "E15.25.0.7", {"start": v(10.63, 34.64) * mm, "end": v(12.42, 30.8) * mm});
            skArc(sketch, "E15.25.0.8", {"start": v(12.57, 30.13) * mm, "mid": v(12.54, 30.47) * mm, "end": v(12.42, 30.8) * mm});
            skLineSegment(sketch, "E15.25.0.9", {"start": v(12.57, 30.13) * mm, "end": v(12.57, 25.4) * mm});
            skLineSegment(sketch, "E15.26.0.0", {"start": v(12.57, 25.4) * mm, "end": v(20.2, 25.4) * mm});
            skLineSegment(sketch, "E15.26.0.1", {"start": v(20.2, 30.13) * mm, "end": v(20.2, 25.4) * mm});
            skArc(sketch, "E15.26.0.2", {"start": v(20.34, 30.8) * mm, "mid": v(20.23, 30.47) * mm, "end": v(20.2, 30.13) * mm});
            skLineSegment(sketch, "E15.26.0.3", {"start": v(20.34, 30.8) * mm, "end": v(22.13, 34.64) * mm});
            skArc(sketch, "E15.26.0.4", {"start": v(23.57, 35.56) * mm, "mid": v(22.72, 35.31) * mm, "end": v(22.13, 34.64) * mm});
            skLineSegment(sketch, "E15.26.0.5", {"start": v(23.57, 35.56) * mm, "end": v(24.43, 35.56) * mm});
            skArc(sketch, "E15.26.0.6", {"start": v(25.87, 34.64) * mm, "mid": v(25.29, 35.31) * mm, "end": v(24.43, 35.56) * mm});
            skLineSegment(sketch, "E15.26.0.7", {"start": v(25.87, 34.64) * mm, "end": v(27.66, 30.8) * mm});
            skArc(sketch, "E15.26.0.8", {"start": v(27.81, 30.13) * mm, "mid": v(27.78, 30.47) * mm, "end": v(27.66, 30.8) * mm});
            skLineSegment(sketch, "E15.26.0.9", {"start": v(27.81, 30.13) * mm, "end": v(27.81, 25.4) * mm});
            skLineSegment(sketch, "E15.27.0.0", {"start": v(27.81, 25.4) * mm, "end": v(35.43, 25.4) * mm});
            skLineSegment(sketch, "E15.27.0.1", {"start": v(35.43, 30.13) * mm, "end": v(35.43, 25.4) * mm});
            skArc(sketch, "E15.27.0.2", {"start": v(35.58, 30.8) * mm, "mid": v(35.47, 30.47) * mm, "end": v(35.43, 30.13) * mm});
            skLineSegment(sketch, "E15.27.0.3", {"start": v(35.58, 30.8) * mm, "end": v(37.37, 34.64) * mm});
            skArc(sketch, "E15.27.0.4", {"start": v(38.81, 35.56) * mm, "mid": v(37.96, 35.31) * mm, "end": v(37.37, 34.64) * mm});
            skLineSegment(sketch, "E15.27.0.5", {"start": v(38.81, 35.56) * mm, "end": v(39.67, 35.56) * mm});
            skArc(sketch, "E15.27.0.6", {"start": v(41.11, 34.64) * mm, "mid": v(40.53, 35.31) * mm, "end": v(39.67, 35.56) * mm});
            skLineSegment(sketch, "E15.27.0.7", {"start": v(41.11, 34.64) * mm, "end": v(42.9, 30.8) * mm});
            skArc(sketch, "E15.27.0.8", {"start": v(43.05, 30.13) * mm, "mid": v(43.02, 30.47) * mm, "end": v(42.9, 30.8) * mm});
            skLineSegment(sketch, "E15.27.0.9", {"start": v(43.05, 30.13) * mm, "end": v(43.05, 25.4) * mm});
            skLineSegment(sketch, "E15.28.0.0", {"start": v(43.05, 25.4) * mm, "end": v(50.67, 25.4) * mm});
            skLineSegment(sketch, "E15.28.0.1", {"start": v(50.67, 30.13) * mm, "end": v(50.67, 25.4) * mm});
            skArc(sketch, "E15.28.0.2", {"start": v(50.82, 30.8) * mm, "mid": v(50.71, 30.47) * mm, "end": v(50.67, 30.13) * mm});
            skLineSegment(sketch, "E15.28.0.3", {"start": v(50.82, 30.8) * mm, "end": v(52.61, 34.64) * mm});
            skArc(sketch, "E15.28.0.4", {"start": v(54.05, 35.56) * mm, "mid": v(53.2, 35.31) * mm, "end": v(52.61, 34.64) * mm});
            skLineSegment(sketch, "E15.28.0.5", {"start": v(54.05, 35.56) * mm, "end": v(54.91, 35.56) * mm});
            skArc(sketch, "E15.28.0.6", {"start": v(56.35, 34.64) * mm, "mid": v(55.77, 35.31) * mm, "end": v(54.91, 35.56) * mm});
            skLineSegment(sketch, "E15.28.0.7", {"start": v(56.35, 34.64) * mm, "end": v(58.14, 30.8) * mm});
            skArc(sketch, "E15.28.0.8", {"start": v(58.3, 30.13) * mm, "mid": v(58.26, 30.47) * mm, "end": v(58.14, 30.8) * mm});
            skLineSegment(sketch, "E15.28.0.9", {"start": v(58.3, 30.13) * mm, "end": v(58.3, 25.4) * mm});
            skLineSegment(sketch, "E15.29.0.0", {"start": v(58.3, 25.4) * mm, "end": v(65.91, 25.4) * mm});
            skLineSegment(sketch, "E15.29.0.1", {"start": v(65.91, 30.13) * mm, "end": v(65.91, 25.4) * mm});
            skArc(sketch, "E15.29.0.2", {"start": v(66.06, 30.8) * mm, "mid": v(65.95, 30.47) * mm, "end": v(65.91, 30.13) * mm});
            skLineSegment(sketch, "E15.29.0.3", {"start": v(66.06, 30.8) * mm, "end": v(67.85, 34.64) * mm});
            skArc(sketch, "E15.29.0.4", {"start": v(69.3, 35.56) * mm, "mid": v(68.44, 35.31) * mm, "end": v(67.85, 34.64) * mm});
            skLineSegment(sketch, "E15.29.0.5", {"start": v(69.3, 35.56) * mm, "end": v(70.15, 35.56) * mm});
            skArc(sketch, "E15.29.0.6", {"start": v(71.6, 34.64) * mm, "mid": v(71, 35.31) * mm, "end": v(70.15, 35.56) * mm});
            skLineSegment(sketch, "E15.29.0.7", {"start": v(71.6, 34.64) * mm, "end": v(73.38, 30.8) * mm});
            skArc(sketch, "E15.29.0.8", {"start": v(73.53, 30.13) * mm, "mid": v(73.5, 30.47) * mm, "end": v(73.38, 30.8) * mm});
            skLineSegment(sketch, "E15.29.0.9", {"start": v(73.53, 30.13) * mm, "end": v(73.53, 25.4) * mm});
            skLineSegment(sketch, "E16.0.30.0", {"start": v(73.53, 25.4) * mm, "end": v(81.15, 25.4) * mm});
            skLineSegment(sketch, "E16.3.30.0", {"start": v(81.15, 30.13) * mm, "end": v(81.15, 25.4) * mm});
            skArc(sketch, "E16.6.30.0", {"start": v(81.3, 30.8) * mm, "mid": v(81.2, 30.47) * mm, "end": v(81.15, 30.13) * mm});
            skLineSegment(sketch, "E16.10.30.0", {"start": v(81.3, 30.8) * mm, "end": v(83.1, 34.64) * mm});
            skArc(sketch, "E16.13.30.0", {"start": v(84.53, 35.56) * mm, "mid": v(83.68, 35.31) * mm, "end": v(83.1, 34.64) * mm});
            skLineSegment(sketch, "E16.17.30.0", {"start": v(84.53, 35.56) * mm, "end": v(85.4, 35.56) * mm});
            skArc(sketch, "E16.20.30.0", {"start": v(86.83, 34.64) * mm, "mid": v(86.25, 35.31) * mm, "end": v(85.4, 35.56) * mm});
            skLineSegment(sketch, "E16.24.30.0", {"start": v(86.83, 34.64) * mm, "end": v(88.62, 30.8) * mm});
            skArc(sketch, "E16.27.30.0", {"start": v(88.77, 30.13) * mm, "mid": v(88.74, 30.47) * mm, "end": v(88.62, 30.8) * mm});
            skLineSegment(sketch, "E16.31.30.0", {"start": v(88.77, 30.13) * mm, "end": v(88.77, 25.4) * mm});
            skLineSegment(sketch, "E16.0.31.0", {"start": v(88.77, 25.4) * mm, "end": v(96.4, 25.4) * mm});
            skLineSegment(sketch, "E16.3.31.0", {"start": v(96.4, 30.13) * mm, "end": v(96.4, 25.4) * mm});
            skArc(sketch, "E16.6.31.0", {"start": v(96.54, 30.8) * mm, "mid": v(96.43, 30.47) * mm, "end": v(96.4, 30.13) * mm});
            skLineSegment(sketch, "E16.10.31.0", {"start": v(96.54, 30.8) * mm, "end": v(98.33, 34.64) * mm});
            skArc(sketch, "E16.13.31.0", {"start": v(99.77, 35.56) * mm, "mid": v(98.92, 35.31) * mm, "end": v(98.33, 34.64) * mm});
            skLineSegment(sketch, "E16.17.31.0", {"start": v(99.77, 35.56) * mm, "end": v(100.63, 35.56) * mm});
            skArc(sketch, "E16.20.31.0", {"start": v(102.07, 34.64) * mm, "mid": v(101.49, 35.31) * mm, "end": v(100.63, 35.56) * mm});
            skLineSegment(sketch, "E16.24.31.0", {"start": v(102.07, 34.64) * mm, "end": v(103.86, 30.8) * mm});
            skArc(sketch, "E16.27.31.0", {"start": v(104.01, 30.13) * mm, "mid": v(103.98, 30.47) * mm, "end": v(103.86, 30.8) * mm});
            skLineSegment(sketch, "E16.31.31.0", {"start": v(104.01, 30.13) * mm, "end": v(104.01, 25.4) * mm});
            skLineSegment(sketch, "E16.0.32.0", {"start": v(104.01, 25.4) * mm, "end": v(111.63, 25.4) * mm});
            skLineSegment(sketch, "E16.3.32.0", {"start": v(111.63, 30.13) * mm, "end": v(111.63, 25.4) * mm});
            skArc(sketch, "E16.6.32.0", {"start": v(111.78, 30.8) * mm, "mid": v(111.67, 30.47) * mm, "end": v(111.63, 30.13) * mm});
            skLineSegment(sketch, "E16.10.32.0", {"start": v(111.78, 30.8) * mm, "end": v(113.57, 34.64) * mm});
            skArc(sketch, "E16.13.32.0", {"start": v(115.01, 35.56) * mm, "mid": v(114.16, 35.31) * mm, "end": v(113.57, 34.64) * mm});
            skLineSegment(sketch, "E16.17.32.0", {"start": v(115.01, 35.56) * mm, "end": v(115.87, 35.56) * mm});
            skArc(sketch, "E16.20.32.0", {"start": v(117.31, 34.64) * mm, "mid": v(116.73, 35.31) * mm, "end": v(115.87, 35.56) * mm});
            skLineSegment(sketch, "E16.24.32.0", {"start": v(117.31, 34.64) * mm, "end": v(119.1, 30.8) * mm});
            skArc(sketch, "E16.27.32.0", {"start": v(119.25, 30.13) * mm, "mid": v(119.22, 30.47) * mm, "end": v(119.1, 30.8) * mm});
            skLineSegment(sketch, "E16.31.32.0", {"start": v(119.25, 30.13) * mm, "end": v(119.25, 25.4) * mm});
            skLineSegment(sketch, "E16.0.33.0", {"start": v(119.25, 25.4) * mm, "end": v(126.87, 25.4) * mm});
            skLineSegment(sketch, "E16.3.33.0", {"start": v(126.87, 30.13) * mm, "end": v(126.87, 25.4) * mm});
            skArc(sketch, "E16.6.33.0", {"start": v(127.02, 30.8) * mm, "mid": v(126.91, 30.47) * mm, "end": v(126.87, 30.13) * mm});
            skLineSegment(sketch, "E16.10.33.0", {"start": v(127.02, 30.8) * mm, "end": v(128.81, 34.64) * mm});
            skArc(sketch, "E16.13.33.0", {"start": v(130.25, 35.56) * mm, "mid": v(129.4, 35.31) * mm, "end": v(128.81, 34.64) * mm});
            skLineSegment(sketch, "E16.17.33.0", {"start": v(130.25, 35.56) * mm, "end": v(131.11, 35.56) * mm});
            skArc(sketch, "E16.20.33.0", {"start": v(132.55, 34.64) * mm, "mid": v(131.97, 35.31) * mm, "end": v(131.11, 35.56) * mm});
            skLineSegment(sketch, "E16.24.33.0", {"start": v(132.55, 34.64) * mm, "end": v(134.34, 30.8) * mm});
            skArc(sketch, "E16.27.33.0", {"start": v(134.5, 30.13) * mm, "mid": v(134.46, 30.47) * mm, "end": v(134.34, 30.8) * mm});
            skLineSegment(sketch, "E16.31.33.0", {"start": v(134.5, 30.13) * mm, "end": v(134.5, 25.4) * mm});
            skLineSegment(sketch, "E16.0.34.0", {"start": v(134.5, 25.4) * mm, "end": v(142.11, 25.4) * mm});
            skLineSegment(sketch, "E16.3.34.0", {"start": v(142.11, 30.13) * mm, "end": v(142.11, 25.4) * mm});
            skArc(sketch, "E16.6.34.0", {"start": v(142.26, 30.8) * mm, "mid": v(142.15, 30.47) * mm, "end": v(142.11, 30.13) * mm});
            skLineSegment(sketch, "E16.10.34.0", {"start": v(142.26, 30.8) * mm, "end": v(144.05, 34.64) * mm});
            skArc(sketch, "E16.13.34.0", {"start": v(145.5, 35.56) * mm, "mid": v(144.64, 35.31) * mm, "end": v(144.05, 34.64) * mm});
            skLineSegment(sketch, "E16.17.34.0", {"start": v(145.5, 35.56) * mm, "end": v(146.35, 35.56) * mm});
            skArc(sketch, "E16.20.34.0", {"start": v(147.8, 34.64) * mm, "mid": v(147.2, 35.31) * mm, "end": v(146.35, 35.56) * mm});
            skLineSegment(sketch, "E16.24.34.0", {"start": v(147.8, 34.64) * mm, "end": v(149.58, 30.8) * mm});
            skArc(sketch, "E16.27.34.0", {"start": v(149.73, 30.13) * mm, "mid": v(149.7, 30.47) * mm, "end": v(149.58, 30.8) * mm});
            skLineSegment(sketch, "E16.31.34.0", {"start": v(149.73, 30.13) * mm, "end": v(149.73, 25.4) * mm});
            skLineSegment(sketch, "E16.0.35.0", {"start": v(149.73, 25.4) * mm, "end": v(157.35, 25.4) * mm});
            skLineSegment(sketch, "E16.3.35.0", {"start": v(157.35, 30.13) * mm, "end": v(157.35, 25.4) * mm});
            skArc(sketch, "E16.6.35.0", {"start": v(157.5, 30.8) * mm, "mid": v(157.4, 30.47) * mm, "end": v(157.35, 30.13) * mm});
            skLineSegment(sketch, "E16.10.35.0", {"start": v(157.5, 30.8) * mm, "end": v(159.3, 34.64) * mm});
            skArc(sketch, "E16.13.35.0", {"start": v(160.73, 35.56) * mm, "mid": v(159.88, 35.31) * mm, "end": v(159.3, 34.64) * mm});
            skLineSegment(sketch, "E16.17.35.0", {"start": v(160.73, 35.56) * mm, "end": v(161.6, 35.56) * mm});
            skArc(sketch, "E16.20.35.0", {"start": v(163.03, 34.64) * mm, "mid": v(162.45, 35.31) * mm, "end": v(161.6, 35.56) * mm});
            skLineSegment(sketch, "E16.24.35.0", {"start": v(163.03, 34.64) * mm, "end": v(164.82, 30.8) * mm});
            skArc(sketch, "E16.27.35.0", {"start": v(164.97, 30.13) * mm, "mid": v(164.94, 30.47) * mm, "end": v(164.82, 30.8) * mm});
            skLineSegment(sketch, "E16.31.35.0", {"start": v(164.97, 30.13) * mm, "end": v(164.97, 25.4) * mm});
            skLineSegment(sketch, "E16.0.36.0", {"start": v(164.97, 25.4) * mm, "end": v(172.6, 25.4) * mm});
            skLineSegment(sketch, "E16.3.36.0", {"start": v(172.6, 30.13) * mm, "end": v(172.6, 25.4) * mm});
            skArc(sketch, "E16.6.36.0", {"start": v(172.74, 30.8) * mm, "mid": v(172.63, 30.47) * mm, "end": v(172.6, 30.13) * mm});
            skLineSegment(sketch, "E16.10.36.0", {"start": v(172.74, 30.8) * mm, "end": v(174.53, 34.64) * mm});
            skArc(sketch, "E16.13.36.0", {"start": v(175.97, 35.56) * mm, "mid": v(175.12, 35.31) * mm, "end": v(174.53, 34.64) * mm});
            skLineSegment(sketch, "E16.17.36.0", {"start": v(175.97, 35.56) * mm, "end": v(176.83, 35.56) * mm});
            skArc(sketch, "E16.20.36.0", {"start": v(178.27, 34.64) * mm, "mid": v(177.69, 35.31) * mm, "end": v(176.83, 35.56) * mm});
            skLineSegment(sketch, "E16.24.36.0", {"start": v(178.27, 34.64) * mm, "end": v(180.06, 30.8) * mm});
            skArc(sketch, "E16.27.36.0", {"start": v(180.21, 30.13) * mm, "mid": v(180.18, 30.47) * mm, "end": v(180.06, 30.8) * mm});
            skLineSegment(sketch, "E16.31.36.0", {"start": v(180.21, 30.13) * mm, "end": v(180.21, 25.4) * mm});
            skLineSegment(sketch, "E16.0.37.0", {"start": v(180.21, 25.4) * mm, "end": v(187.83, 25.4) * mm});
            skLineSegment(sketch, "E16.3.37.0", {"start": v(187.83, 30.13) * mm, "end": v(187.83, 25.4) * mm});
            skArc(sketch, "E16.6.37.0", {"start": v(187.98, 30.8) * mm, "mid": v(187.87, 30.47) * mm, "end": v(187.83, 30.13) * mm});
            skLineSegment(sketch, "E16.10.37.0", {"start": v(187.98, 30.8) * mm, "end": v(189.77, 34.64) * mm});
            skArc(sketch, "E16.13.37.0", {"start": v(191.21, 35.56) * mm, "mid": v(190.36, 35.31) * mm, "end": v(189.77, 34.64) * mm});
            skLineSegment(sketch, "E16.17.37.0", {"start": v(191.21, 35.56) * mm, "end": v(192.07, 35.56) * mm});
            skArc(sketch, "E16.20.37.0", {"start": v(193.51, 34.64) * mm, "mid": v(192.93, 35.31) * mm, "end": v(192.07, 35.56) * mm});
            skLineSegment(sketch, "E16.24.37.0", {"start": v(193.51, 34.64) * mm, "end": v(195.3, 30.8) * mm});
            skArc(sketch, "E16.27.37.0", {"start": v(195.45, 30.13) * mm, "mid": v(195.42, 30.47) * mm, "end": v(195.3, 30.8) * mm});
            skLineSegment(sketch, "E16.31.37.0", {"start": v(195.45, 30.13) * mm, "end": v(195.45, 25.4) * mm});
            skLineSegment(sketch, "E16.0.38.0", {"start": v(195.45, 25.4) * mm, "end": v(203.07, 25.4) * mm});
            skLineSegment(sketch, "E16.3.38.0", {"start": v(203.07, 30.13) * mm, "end": v(203.07, 25.4) * mm});
            skArc(sketch, "E16.6.38.0", {"start": v(203.22, 30.8) * mm, "mid": v(203.11, 30.47) * mm, "end": v(203.07, 30.13) * mm});
            skLineSegment(sketch, "E16.10.38.0", {"start": v(203.22, 30.8) * mm, "end": v(205.01, 34.64) * mm});
            skArc(sketch, "E16.13.38.0", {"start": v(206.45, 35.56) * mm, "mid": v(205.6, 35.31) * mm, "end": v(205.01, 34.64) * mm});
            skLineSegment(sketch, "E16.17.38.0", {"start": v(206.45, 35.56) * mm, "end": v(207.31, 35.56) * mm});
            skArc(sketch, "E16.20.38.0", {"start": v(208.75, 34.64) * mm, "mid": v(208.17, 35.31) * mm, "end": v(207.31, 35.56) * mm});
            skLineSegment(sketch, "E16.24.38.0", {"start": v(208.75, 34.64) * mm, "end": v(210.54, 30.8) * mm});
            skArc(sketch, "E16.27.38.0", {"start": v(210.7, 30.13) * mm, "mid": v(210.66, 30.47) * mm, "end": v(210.54, 30.8) * mm});
            skLineSegment(sketch, "E16.31.38.0", {"start": v(210.7, 30.13) * mm, "end": v(210.7, 25.4) * mm});
            skLineSegment(sketch, "E16.0.39.0", {"start": v(210.7, 25.4) * mm, "end": v(218.31, 25.4) * mm});
            skLineSegment(sketch, "E16.3.39.0", {"start": v(218.31, 30.13) * mm, "end": v(218.31, 25.4) * mm});
            skArc(sketch, "E16.6.39.0", {"start": v(218.46, 30.8) * mm, "mid": v(218.35, 30.47) * mm, "end": v(218.31, 30.13) * mm});
            skLineSegment(sketch, "E16.10.39.0", {"start": v(218.46, 30.8) * mm, "end": v(220.25, 34.64) * mm});
            skArc(sketch, "E16.13.39.0", {"start": v(221.7, 35.56) * mm, "mid": v(220.84, 35.31) * mm, "end": v(220.25, 34.64) * mm});
            skLineSegment(sketch, "E16.17.39.0", {"start": v(221.7, 35.56) * mm, "end": v(222.55, 35.56) * mm});
            skArc(sketch, "E16.20.39.0", {"start": v(224, 34.64) * mm, "mid": v(223.4, 35.31) * mm, "end": v(222.55, 35.56) * mm});
            skLineSegment(sketch, "E16.24.39.0", {"start": v(224, 34.64) * mm, "end": v(225.78, 30.8) * mm});
            skArc(sketch, "E16.27.39.0", {"start": v(225.93, 30.13) * mm, "mid": v(225.9, 30.47) * mm, "end": v(225.78, 30.8) * mm});
            skLineSegment(sketch, "E16.31.39.0", {"start": v(225.93, 30.13) * mm, "end": v(225.93, 25.4) * mm});
            skLineSegment(sketch, "E16.0.40.0", {"start": v(225.93, 25.4) * mm, "end": v(233.55, 25.4) * mm});
            skLineSegment(sketch, "E16.3.40.0", {"start": v(233.55, 30.13) * mm, "end": v(233.55, 25.4) * mm});
            skArc(sketch, "E16.6.40.0", {"start": v(233.7, 30.8) * mm, "mid": v(233.6, 30.47) * mm, "end": v(233.55, 30.13) * mm});
            skLineSegment(sketch, "E16.10.40.0", {"start": v(233.7, 30.8) * mm, "end": v(235.5, 34.64) * mm});
            skArc(sketch, "E16.13.40.0", {"start": v(236.93, 35.56) * mm, "mid": v(236.08, 35.31) * mm, "end": v(235.5, 34.64) * mm});
            skLineSegment(sketch, "E16.17.40.0", {"start": v(236.93, 35.56) * mm, "end": v(237.8, 35.56) * mm});
            skArc(sketch, "E16.20.40.0", {"start": v(239.23, 34.64) * mm, "mid": v(238.65, 35.31) * mm, "end": v(237.8, 35.56) * mm});
            skLineSegment(sketch, "E16.24.40.0", {"start": v(239.23, 34.64) * mm, "end": v(241.02, 30.8) * mm});
            skArc(sketch, "E16.27.40.0", {"start": v(241.17, 30.13) * mm, "mid": v(241.14, 30.47) * mm, "end": v(241.02, 30.8) * mm});
            skLineSegment(sketch, "E16.31.40.0", {"start": v(241.17, 30.13) * mm, "end": v(241.17, 25.4) * mm});
            skLineSegment(sketch, "E16.0.41.0", {"start": v(241.17, 25.4) * mm, "end": v(248.8, 25.4) * mm});
            skLineSegment(sketch, "E16.3.41.0", {"start": v(248.8, 30.13) * mm, "end": v(248.8, 25.4) * mm});
            skArc(sketch, "E16.6.41.0", {"start": v(248.94, 30.8) * mm, "mid": v(248.83, 30.47) * mm, "end": v(248.8, 30.13) * mm});
            skLineSegment(sketch, "E16.10.41.0", {"start": v(248.94, 30.8) * mm, "end": v(250.73, 34.64) * mm});
            skArc(sketch, "E16.13.41.0", {"start": v(252.17, 35.56) * mm, "mid": v(251.32, 35.31) * mm, "end": v(250.73, 34.64) * mm});
            skLineSegment(sketch, "E16.17.41.0", {"start": v(252.17, 35.56) * mm, "end": v(253.03, 35.56) * mm});
            skArc(sketch, "E16.20.41.0", {"start": v(254.47, 34.64) * mm, "mid": v(253.89, 35.31) * mm, "end": v(253.03, 35.56) * mm});
            skLineSegment(sketch, "E16.24.41.0", {"start": v(254.47, 34.64) * mm, "end": v(256.26, 30.8) * mm});
            skArc(sketch, "E16.27.41.0", {"start": v(256.41, 30.13) * mm, "mid": v(256.38, 30.47) * mm, "end": v(256.26, 30.8) * mm});
            skLineSegment(sketch, "E16.31.41.0", {"start": v(256.41, 30.13) * mm, "end": v(256.41, 25.4) * mm});
            skLineSegment(sketch, "E16.0.42.0", {"start": v(256.41, 25.4) * mm, "end": v(264.03, 25.4) * mm});
            skLineSegment(sketch, "E16.3.42.0", {"start": v(264.03, 30.13) * mm, "end": v(264.03, 25.4) * mm});
            skArc(sketch, "E16.6.42.0", {"start": v(264.18, 30.8) * mm, "mid": v(264.07, 30.47) * mm, "end": v(264.03, 30.13) * mm});
            skLineSegment(sketch, "E16.10.42.0", {"start": v(264.18, 30.8) * mm, "end": v(265.97, 34.64) * mm});
            skArc(sketch, "E16.13.42.0", {"start": v(267.41, 35.56) * mm, "mid": v(266.56, 35.31) * mm, "end": v(265.97, 34.64) * mm});
            skLineSegment(sketch, "E16.17.42.0", {"start": v(267.41, 35.56) * mm, "end": v(268.27, 35.56) * mm});
            skArc(sketch, "E16.20.42.0", {"start": v(269.71, 34.64) * mm, "mid": v(269.13, 35.31) * mm, "end": v(268.27, 35.56) * mm});
            skLineSegment(sketch, "E16.24.42.0", {"start": v(269.71, 34.64) * mm, "end": v(271.5, 30.8) * mm});
            skArc(sketch, "E16.27.42.0", {"start": v(271.65, 30.13) * mm, "mid": v(271.62, 30.47) * mm, "end": v(271.5, 30.8) * mm});
            skLineSegment(sketch, "E16.31.42.0", {"start": v(271.65, 30.13) * mm, "end": v(271.65, 25.4) * mm});
            skLineSegment(sketch, "E16.0.43.0", {"start": v(271.65, 25.4) * mm, "end": v(279.27, 25.4) * mm});
            skLineSegment(sketch, "E16.3.43.0", {"start": v(279.27, 30.13) * mm, "end": v(279.27, 25.4) * mm});
            skArc(sketch, "E16.6.43.0", {"start": v(279.42, 30.8) * mm, "mid": v(279.31, 30.47) * mm, "end": v(279.27, 30.13) * mm});
            skLineSegment(sketch, "E16.10.43.0", {"start": v(279.42, 30.8) * mm, "end": v(281.21, 34.64) * mm});
            skArc(sketch, "E16.13.43.0", {"start": v(282.65, 35.56) * mm, "mid": v(281.8, 35.31) * mm, "end": v(281.21, 34.64) * mm});
            skLineSegment(sketch, "E16.17.43.0", {"start": v(282.65, 35.56) * mm, "end": v(283.51, 35.56) * mm});
            skArc(sketch, "E16.20.43.0", {"start": v(284.95, 34.64) * mm, "mid": v(284.37, 35.31) * mm, "end": v(283.51, 35.56) * mm});
            skLineSegment(sketch, "E16.24.43.0", {"start": v(284.95, 34.64) * mm, "end": v(286.74, 30.8) * mm});
            skArc(sketch, "E16.27.43.0", {"start": v(286.9, 30.13) * mm, "mid": v(286.86, 30.47) * mm, "end": v(286.74, 30.8) * mm});
            skLineSegment(sketch, "E16.31.43.0", {"start": v(286.9, 30.13) * mm, "end": v(286.9, 25.4) * mm});
            skLineSegment(sketch, "E16.0.44.0", {"start": v(286.9, 25.4) * mm, "end": v(294.51, 25.4) * mm});
            skLineSegment(sketch, "E16.3.44.0", {"start": v(294.51, 30.13) * mm, "end": v(294.51, 25.4) * mm});
            skArc(sketch, "E16.6.44.0", {"start": v(294.66, 30.8) * mm, "mid": v(294.55, 30.47) * mm, "end": v(294.51, 30.13) * mm});
            skLineSegment(sketch, "E16.10.44.0", {"start": v(294.66, 30.8) * mm, "end": v(296.45, 34.64) * mm});
            skArc(sketch, "E16.13.44.0", {"start": v(297.9, 35.56) * mm, "mid": v(297.04, 35.31) * mm, "end": v(296.45, 34.64) * mm});
            skLineSegment(sketch, "E16.17.44.0", {"start": v(297.9, 35.56) * mm, "end": v(298.75, 35.56) * mm});
            skArc(sketch, "E16.20.44.0", {"start": v(300.2, 34.64) * mm, "mid": v(299.6, 35.31) * mm, "end": v(298.75, 35.56) * mm});
            skLineSegment(sketch, "E16.24.44.0", {"start": v(300.2, 34.64) * mm, "end": v(301.98, 30.8) * mm});
            skArc(sketch, "E16.27.44.0", {"start": v(302.13, 30.13) * mm, "mid": v(302.1, 30.47) * mm, "end": v(301.98, 30.8) * mm});
            skLineSegment(sketch, "E16.31.44.0", {"start": v(302.13, 30.13) * mm, "end": v(302.13, 25.4) * mm});
            skLineSegment(sketch, "E16.0.45.0", {"start": v(302.13, 25.4) * mm, "end": v(309.75, 25.4) * mm});
            skLineSegment(sketch, "E16.3.45.0", {"start": v(309.75, 30.13) * mm, "end": v(309.75, 25.4) * mm});
            skArc(sketch, "E16.6.45.0", {"start": v(309.9, 30.8) * mm, "mid": v(309.8, 30.47) * mm, "end": v(309.75, 30.13) * mm});
            skLineSegment(sketch, "E16.10.45.0", {"start": v(309.9, 30.8) * mm, "end": v(311.7, 34.64) * mm});
            skArc(sketch, "E16.13.45.0", {"start": v(313.13, 35.56) * mm, "mid": v(312.28, 35.31) * mm, "end": v(311.7, 34.64) * mm});
            skLineSegment(sketch, "E16.17.45.0", {"start": v(313.13, 35.56) * mm, "end": v(314, 35.56) * mm});
            skArc(sketch, "E16.20.45.0", {"start": v(315.43, 34.64) * mm, "mid": v(314.85, 35.31) * mm, "end": v(314, 35.56) * mm});
            skLineSegment(sketch, "E16.24.45.0", {"start": v(315.43, 34.64) * mm, "end": v(317.22, 30.8) * mm});
            skArc(sketch, "E16.27.45.0", {"start": v(317.37, 30.13) * mm, "mid": v(317.34, 30.47) * mm, "end": v(317.22, 30.8) * mm});
            skLineSegment(sketch, "E16.31.45.0", {"start": v(317.37, 30.13) * mm, "end": v(317.37, 25.4) * mm});
            skLineSegment(sketch, "E16.0.46.0", {"start": v(317.37, 25.4) * mm, "end": v(325, 25.4) * mm});
            skLineSegment(sketch, "E16.3.46.0", {"start": v(325, 30.13) * mm, "end": v(325, 25.4) * mm});
            skArc(sketch, "E16.6.46.0", {"start": v(325.14, 30.8) * mm, "mid": v(325.03, 30.47) * mm, "end": v(325, 30.13) * mm});
            skLineSegment(sketch, "E16.10.46.0", {"start": v(325.14, 30.8) * mm, "end": v(326.93, 34.64) * mm});
            skArc(sketch, "E16.13.46.0", {"start": v(328.37, 35.56) * mm, "mid": v(327.52, 35.31) * mm, "end": v(326.93, 34.64) * mm});
            skLineSegment(sketch, "E16.17.46.0", {"start": v(328.37, 35.56) * mm, "end": v(329.23, 35.56) * mm});
            skArc(sketch, "E16.20.46.0", {"start": v(330.67, 34.64) * mm, "mid": v(330.09, 35.31) * mm, "end": v(329.23, 35.56) * mm});
            skLineSegment(sketch, "E16.24.46.0", {"start": v(330.67, 34.64) * mm, "end": v(332.46, 30.8) * mm});
            skArc(sketch, "E16.27.46.0", {"start": v(332.61, 30.13) * mm, "mid": v(332.58, 30.47) * mm, "end": v(332.46, 30.8) * mm});
            skLineSegment(sketch, "E16.31.46.0", {"start": v(332.61, 30.13) * mm, "end": v(332.61, 25.4) * mm});
            skLineSegment(sketch, "E16.0.47.0", {"start": v(332.61, 25.4) * mm, "end": v(340.23, 25.4) * mm});
            skLineSegment(sketch, "E16.3.47.0", {"start": v(340.23, 30.13) * mm, "end": v(340.23, 25.4) * mm});
            skArc(sketch, "E16.6.47.0", {"start": v(340.38, 30.8) * mm, "mid": v(340.27, 30.47) * mm, "end": v(340.23, 30.13) * mm});
            skLineSegment(sketch, "E16.10.47.0", {"start": v(340.38, 30.8) * mm, "end": v(342.17, 34.64) * mm});
            skArc(sketch, "E16.13.47.0", {"start": v(343.61, 35.56) * mm, "mid": v(342.76, 35.31) * mm, "end": v(342.17, 34.64) * mm});
            skLineSegment(sketch, "E16.17.47.0", {"start": v(343.61, 35.56) * mm, "end": v(344.47, 35.56) * mm});
            skArc(sketch, "E16.20.47.0", {"start": v(345.91, 34.64) * mm, "mid": v(345.33, 35.31) * mm, "end": v(344.47, 35.56) * mm});
            skLineSegment(sketch, "E16.24.47.0", {"start": v(345.91, 34.64) * mm, "end": v(347.7, 30.8) * mm});
            skArc(sketch, "E16.27.47.0", {"start": v(347.85, 30.13) * mm, "mid": v(347.82, 30.47) * mm, "end": v(347.7, 30.8) * mm});
            skLineSegment(sketch, "E16.31.47.0", {"start": v(347.85, 30.13) * mm, "end": v(347.85, 25.4) * mm});
            skLineSegment(sketch, "E16.0.48.0", {"start": v(347.85, 25.4) * mm, "end": v(355.47, 25.4) * mm});
            skLineSegment(sketch, "E16.3.48.0", {"start": v(355.47, 30.13) * mm, "end": v(355.47, 25.4) * mm});
            skArc(sketch, "E16.6.48.0", {"start": v(355.62, 30.8) * mm, "mid": v(355.51, 30.47) * mm, "end": v(355.47, 30.13) * mm});
            skLineSegment(sketch, "E16.10.48.0", {"start": v(355.62, 30.8) * mm, "end": v(357.41, 34.64) * mm});
            skArc(sketch, "E16.13.48.0", {"start": v(358.85, 35.56) * mm, "mid": v(358, 35.31) * mm, "end": v(357.41, 34.64) * mm});
            skLineSegment(sketch, "E16.17.48.0", {"start": v(358.85, 35.56) * mm, "end": v(359.71, 35.56) * mm});
            skArc(sketch, "E16.20.48.0", {"start": v(361.15, 34.64) * mm, "mid": v(360.57, 35.31) * mm, "end": v(359.71, 35.56) * mm});
            skLineSegment(sketch, "E16.24.48.0", {"start": v(361.15, 34.64) * mm, "end": v(362.94, 30.8) * mm});
            skArc(sketch, "E16.27.48.0", {"start": v(363.1, 30.13) * mm, "mid": v(363.06, 30.47) * mm, "end": v(362.94, 30.8) * mm});
            skLineSegment(sketch, "E16.31.48.0", {"start": v(363.1, 30.13) * mm, "end": v(363.1, 25.4) * mm});
            skLineSegment(sketch, "E16.0.49.0", {"start": v(363.1, 25.4) * mm, "end": v(370.71, 25.4) * mm});
            skLineSegment(sketch, "E16.3.49.0", {"start": v(370.71, 30.13) * mm, "end": v(370.71, 25.4) * mm});
            skArc(sketch, "E16.6.49.0", {"start": v(370.86, 30.8) * mm, "mid": v(370.75, 30.47) * mm, "end": v(370.71, 30.13) * mm});
            skLineSegment(sketch, "E16.10.49.0", {"start": v(370.86, 30.8) * mm, "end": v(372.65, 34.64) * mm});
            skArc(sketch, "E16.13.49.0", {"start": v(374.1, 35.56) * mm, "mid": v(373.24, 35.31) * mm, "end": v(372.65, 34.64) * mm});
            skLineSegment(sketch, "E16.17.49.0", {"start": v(374.1, 35.56) * mm, "end": v(374.95, 35.56) * mm});
            skArc(sketch, "E16.20.49.0", {"start": v(376.4, 34.64) * mm, "mid": v(375.8, 35.31) * mm, "end": v(374.95, 35.56) * mm});
            skLineSegment(sketch, "E16.24.49.0", {"start": v(376.4, 34.64) * mm, "end": v(378.18, 30.8) * mm});
            skArc(sketch, "E16.27.49.0", {"start": v(378.33, 30.13) * mm, "mid": v(378.3, 30.47) * mm, "end": v(378.18, 30.8) * mm});
            skLineSegment(sketch, "E16.31.49.0", {"start": v(378.33, 30.13) * mm, "end": v(378.33, 25.4) * mm});
            skLineSegment(sketch, "E17", {"start": v(-383.67, 25.4) * mm, "end": v(-383.67, 19.05) * mm});
            skLineSegment(sketch, "E18", {"start": v(-383.67, 19.05) * mm, "end": v(378.33, 19.05) * mm});
            skLineSegment(sketch, "E19", {"start": v(378.33, 19.05) * mm, "end": v(378.4, 24.07) * mm});
            skSolve(sketch);
        }
        {
            var Q0;
            {var subQ49=sQuery(id+"F2.wireOp",EDGE,"E4");Q0=makeQuery(id+"F2.imprint","IMPRINT",FACE,{"disambiguationData":[TD([[makeQuery(id+"F2.imprint","IMPRINT",EDGE,{"derivedFrom":subQ49}),-1.0]])]});}
            var Q1;
            {var subQ0=sQuery(id+"F2.wireOp",EDGE,"E15.1.0.1");Q1=makeQuery(id+"F2.imprint","IMPRINT",FACE,{"disambiguationData":[TD([[makeQuery(id+"F2.imprint","IMPRINT",EDGE,{"derivedFrom":subQ0}),1.0]])]});}
            var Q2;
            Q2=makeQuery(id+"F2.imprint","IMPRINT",FACE,{"disambiguationData":[TD([[makeQuery(id+"F2.imprint","IMPRINT",EDGE,{"derivedFrom":sQuery(id+"F2.wireOp",EDGE,"E6")}),-1.0]])]});
            var Q3;
            {var subQ0=sQuery(id+"F2.wireOp",EDGE,"E15.2.0.1");Q3=makeQuery(id+"F2.imprint","IMPRINT",FACE,{"disambiguationData":[TD([[makeQuery(id+"F2.imprint","IMPRINT",EDGE,{"derivedFrom":subQ0}),1.0]])]});}
            var Q4;
            {var subQ0=sQuery(id+"F2.wireOp",EDGE,"E15.4.0.1");Q4=makeQuery(id+"F2.imprint","IMPRINT",FACE,{"disambiguationData":[TD([[makeQuery(id+"F2.imprint","IMPRINT",EDGE,{"derivedFrom":subQ0}),1.0]])]});}
            var Q5;
            {var subQ0=sQuery(id+"F2.wireOp",EDGE,"E15.3.0.1");Q5=makeQuery(id+"F2.imprint","IMPRINT",FACE,{"disambiguationData":[TD([[makeQuery(id+"F2.imprint","IMPRINT",EDGE,{"derivedFrom":subQ0}),1.0]])]});}
            var Q6;
            {var subQ0=sQuery(id+"F2.wireOp",EDGE,"E15.5.0.1");Q6=makeQuery(id+"F2.imprint","IMPRINT",FACE,{"disambiguationData":[TD([[makeQuery(id+"F2.imprint","IMPRINT",EDGE,{"derivedFrom":subQ0}),1.0]])]});}
            var Q7;
            {var subQ0=sQuery(id+"F2.wireOp",EDGE,"E15.6.0.1");Q7=makeQuery(id+"F2.imprint","IMPRINT",FACE,{"disambiguationData":[TD([[makeQuery(id+"F2.imprint","IMPRINT",EDGE,{"derivedFrom":subQ0}),1.0]])]});}
            var Q8;
            {var subQ0=sQuery(id+"F2.wireOp",EDGE,"E15.7.0.1");Q8=makeQuery(id+"F2.imprint","IMPRINT",FACE,{"disambiguationData":[TD([[makeQuery(id+"F2.imprint","IMPRINT",EDGE,{"derivedFrom":subQ0}),1.0]])]});}
            var Q9;
            {var subQ0=sQuery(id+"F2.wireOp",EDGE,"E15.8.0.1");Q9=makeQuery(id+"F2.imprint","IMPRINT",FACE,{"disambiguationData":[TD([[makeQuery(id+"F2.imprint","IMPRINT",EDGE,{"derivedFrom":subQ0}),1.0]])]});}
            var Q10;
            {var subQ0=sQuery(id+"F2.wireOp",EDGE,"E15.9.0.1");Q10=makeQuery(id+"F2.imprint","IMPRINT",FACE,{"disambiguationData":[TD([[makeQuery(id+"F2.imprint","IMPRINT",EDGE,{"derivedFrom":subQ0}),1.0]])]});}
            var Q11;
            {var subQ0=sQuery(id+"F2.wireOp",EDGE,"E15.10.0.1");Q11=makeQuery(id+"F2.imprint","IMPRINT",FACE,{"disambiguationData":[TD([[makeQuery(id+"F2.imprint","IMPRINT",EDGE,{"derivedFrom":subQ0}),1.0]])]});}
            var Q12;
            {var subQ0=sQuery(id+"F2.wireOp",EDGE,"E15.11.0.1");Q12=makeQuery(id+"F2.imprint","IMPRINT",FACE,{"disambiguationData":[TD([[makeQuery(id+"F2.imprint","IMPRINT",EDGE,{"derivedFrom":subQ0}),1.0]])]});}
            var Q13;
            {var subQ0=sQuery(id+"F2.wireOp",EDGE,"E15.12.0.1");Q13=makeQuery(id+"F2.imprint","IMPRINT",FACE,{"disambiguationData":[TD([[makeQuery(id+"F2.imprint","IMPRINT",EDGE,{"derivedFrom":subQ0}),1.0]])]});}
            var Q14;
            {var subQ0=sQuery(id+"F2.wireOp",EDGE,"E15.13.0.1");Q14=makeQuery(id+"F2.imprint","IMPRINT",FACE,{"disambiguationData":[TD([[makeQuery(id+"F2.imprint","IMPRINT",EDGE,{"derivedFrom":subQ0}),1.0]])]});}
            var Q15;
            {var subQ0=sQuery(id+"F2.wireOp",EDGE,"E15.14.0.1");Q15=makeQuery(id+"F2.imprint","IMPRINT",FACE,{"disambiguationData":[TD([[makeQuery(id+"F2.imprint","IMPRINT",EDGE,{"derivedFrom":subQ0}),1.0]])]});}
            var Q16;
            {var subQ0=sQuery(id+"F2.wireOp",EDGE,"E15.15.0.1");Q16=makeQuery(id+"F2.imprint","IMPRINT",FACE,{"disambiguationData":[TD([[makeQuery(id+"F2.imprint","IMPRINT",EDGE,{"derivedFrom":subQ0}),1.0]])]});}
            var Q17;
            {var subQ0=sQuery(id+"F2.wireOp",EDGE,"E15.16.0.1");Q17=makeQuery(id+"F2.imprint","IMPRINT",FACE,{"disambiguationData":[TD([[makeQuery(id+"F2.imprint","IMPRINT",EDGE,{"derivedFrom":subQ0}),1.0]])]});}
            var Q18;
            {var subQ0=sQuery(id+"F2.wireOp",EDGE,"E15.17.0.1");Q18=makeQuery(id+"F2.imprint","IMPRINT",FACE,{"disambiguationData":[TD([[makeQuery(id+"F2.imprint","IMPRINT",EDGE,{"derivedFrom":subQ0}),1.0]])]});}
            var Q19;
            {var subQ0=sQuery(id+"F2.wireOp",EDGE,"E15.18.0.1");Q19=makeQuery(id+"F2.imprint","IMPRINT",FACE,{"disambiguationData":[TD([[makeQuery(id+"F2.imprint","IMPRINT",EDGE,{"derivedFrom":subQ0}),1.0]])]});}
            var Q20;
            {var subQ0=sQuery(id+"F2.wireOp",EDGE,"E15.19.0.1");Q20=makeQuery(id+"F2.imprint","IMPRINT",FACE,{"disambiguationData":[TD([[makeQuery(id+"F2.imprint","IMPRINT",EDGE,{"derivedFrom":subQ0}),1.0]])]});}
            var Q21;
            {var subQ0=sQuery(id+"F2.wireOp",EDGE,"E15.20.0.1");Q21=makeQuery(id+"F2.imprint","IMPRINT",FACE,{"disambiguationData":[TD([[makeQuery(id+"F2.imprint","IMPRINT",EDGE,{"derivedFrom":subQ0}),1.0]])]});}
            var Q22;
            {var subQ0=sQuery(id+"F2.wireOp",EDGE,"E15.21.0.1");Q22=makeQuery(id+"F2.imprint","IMPRINT",FACE,{"disambiguationData":[TD([[makeQuery(id+"F2.imprint","IMPRINT",EDGE,{"derivedFrom":subQ0}),1.0]])]});}
            var Q23;
            {var subQ0=sQuery(id+"F2.wireOp",EDGE,"E15.22.0.1");Q23=makeQuery(id+"F2.imprint","IMPRINT",FACE,{"disambiguationData":[TD([[makeQuery(id+"F2.imprint","IMPRINT",EDGE,{"derivedFrom":subQ0}),1.0]])]});}
            var Q24;
            {var subQ0=sQuery(id+"F2.wireOp",EDGE,"E15.23.0.1");Q24=makeQuery(id+"F2.imprint","IMPRINT",FACE,{"disambiguationData":[TD([[makeQuery(id+"F2.imprint","IMPRINT",EDGE,{"derivedFrom":subQ0}),1.0]])]});}
            var Q25;
            {var subQ0=sQuery(id+"F2.wireOp",EDGE,"E15.24.0.1");Q25=makeQuery(id+"F2.imprint","IMPRINT",FACE,{"disambiguationData":[TD([[makeQuery(id+"F2.imprint","IMPRINT",EDGE,{"derivedFrom":subQ0}),1.0]])]});}
            var Q26;
            {var subQ0=sQuery(id+"F2.wireOp",EDGE,"E15.25.0.1");Q26=makeQuery(id+"F2.imprint","IMPRINT",FACE,{"disambiguationData":[TD([[makeQuery(id+"F2.imprint","IMPRINT",EDGE,{"derivedFrom":subQ0}),1.0]])]});}
            var Q27;
            {var subQ0=sQuery(id+"F2.wireOp",EDGE,"E15.26.0.1");Q27=makeQuery(id+"F2.imprint","IMPRINT",FACE,{"disambiguationData":[TD([[makeQuery(id+"F2.imprint","IMPRINT",EDGE,{"derivedFrom":subQ0}),1.0]])]});}
            var Q28;
            {var subQ0=sQuery(id+"F2.wireOp",EDGE,"E15.27.0.1");Q28=makeQuery(id+"F2.imprint","IMPRINT",FACE,{"disambiguationData":[TD([[makeQuery(id+"F2.imprint","IMPRINT",EDGE,{"derivedFrom":subQ0}),1.0]])]});}
            var Q29;
            {var subQ0=sQuery(id+"F2.wireOp",EDGE,"E15.29.0.1");Q29=makeQuery(id+"F2.imprint","IMPRINT",FACE,{"disambiguationData":[TD([[makeQuery(id+"F2.imprint","IMPRINT",EDGE,{"derivedFrom":subQ0}),1.0]])]});}
            var Q30;
            {var subQ0=sQuery(id+"F2.wireOp",EDGE,"E15.28.0.1");Q30=makeQuery(id+"F2.imprint","IMPRINT",FACE,{"disambiguationData":[TD([[makeQuery(id+"F2.imprint","IMPRINT",EDGE,{"derivedFrom":subQ0}),1.0]])]});}
            var Q31;
            {var subQ0=sQuery(id+"F2.wireOp",EDGE,"E16.3.30.0");Q31=makeQuery(id+"F2.imprint","IMPRINT",FACE,{"disambiguationData":[TD([[makeQuery(id+"F2.imprint","IMPRINT",EDGE,{"derivedFrom":subQ0}),1.0]])]});}
            var Q32;
            {var subQ0=sQuery(id+"F2.wireOp",EDGE,"E16.3.32.0");Q32=makeQuery(id+"F2.imprint","IMPRINT",FACE,{"disambiguationData":[TD([[makeQuery(id+"F2.imprint","IMPRINT",EDGE,{"derivedFrom":subQ0}),1.0]])]});}
            var Q33;
            {var subQ0=sQuery(id+"F2.wireOp",EDGE,"E16.3.31.0");Q33=makeQuery(id+"F2.imprint","IMPRINT",FACE,{"disambiguationData":[TD([[makeQuery(id+"F2.imprint","IMPRINT",EDGE,{"derivedFrom":subQ0}),1.0]])]});}
            var Q34;
            {var subQ0=sQuery(id+"F2.wireOp",EDGE,"E16.3.33.0");Q34=makeQuery(id+"F2.imprint","IMPRINT",FACE,{"disambiguationData":[TD([[makeQuery(id+"F2.imprint","IMPRINT",EDGE,{"derivedFrom":subQ0}),1.0]])]});}
            var Q35;
            {var subQ0=sQuery(id+"F2.wireOp",EDGE,"E16.3.34.0");Q35=makeQuery(id+"F2.imprint","IMPRINT",FACE,{"disambiguationData":[TD([[makeQuery(id+"F2.imprint","IMPRINT",EDGE,{"derivedFrom":subQ0}),1.0]])]});}
            var Q36;
            {var subQ0=sQuery(id+"F2.wireOp",EDGE,"E16.3.35.0");Q36=makeQuery(id+"F2.imprint","IMPRINT",FACE,{"disambiguationData":[TD([[makeQuery(id+"F2.imprint","IMPRINT",EDGE,{"derivedFrom":subQ0}),1.0]])]});}
            var Q37;
            {var subQ0=sQuery(id+"F2.wireOp",EDGE,"E16.3.36.0");Q37=makeQuery(id+"F2.imprint","IMPRINT",FACE,{"disambiguationData":[TD([[makeQuery(id+"F2.imprint","IMPRINT",EDGE,{"derivedFrom":subQ0}),1.0]])]});}
            var Q38;
            {var subQ0=sQuery(id+"F2.wireOp",EDGE,"E16.3.37.0");Q38=makeQuery(id+"F2.imprint","IMPRINT",FACE,{"disambiguationData":[TD([[makeQuery(id+"F2.imprint","IMPRINT",EDGE,{"derivedFrom":subQ0}),1.0]])]});}
            var Q39;
            {var subQ0=sQuery(id+"F2.wireOp",EDGE,"E16.3.38.0");Q39=makeQuery(id+"F2.imprint","IMPRINT",FACE,{"disambiguationData":[TD([[makeQuery(id+"F2.imprint","IMPRINT",EDGE,{"derivedFrom":subQ0}),1.0]])]});}
            var Q40;
            {var subQ0=sQuery(id+"F2.wireOp",EDGE,"E16.3.39.0");Q40=makeQuery(id+"F2.imprint","IMPRINT",FACE,{"disambiguationData":[TD([[makeQuery(id+"F2.imprint","IMPRINT",EDGE,{"derivedFrom":subQ0}),1.0]])]});}
            var Q41;
            {var subQ0=sQuery(id+"F2.wireOp",EDGE,"E16.3.40.0");Q41=makeQuery(id+"F2.imprint","IMPRINT",FACE,{"disambiguationData":[TD([[makeQuery(id+"F2.imprint","IMPRINT",EDGE,{"derivedFrom":subQ0}),1.0]])]});}
            var Q42;
            {var subQ0=sQuery(id+"F2.wireOp",EDGE,"E16.3.41.0");Q42=makeQuery(id+"F2.imprint","IMPRINT",FACE,{"disambiguationData":[TD([[makeQuery(id+"F2.imprint","IMPRINT",EDGE,{"derivedFrom":subQ0}),1.0]])]});}
            var Q43;
            {var subQ0=sQuery(id+"F2.wireOp",EDGE,"E16.3.42.0");Q43=makeQuery(id+"F2.imprint","IMPRINT",FACE,{"disambiguationData":[TD([[makeQuery(id+"F2.imprint","IMPRINT",EDGE,{"derivedFrom":subQ0}),1.0]])]});}
            var Q44;
            {var subQ0=sQuery(id+"F2.wireOp",EDGE,"E16.3.43.0");Q44=makeQuery(id+"F2.imprint","IMPRINT",FACE,{"disambiguationData":[TD([[makeQuery(id+"F2.imprint","IMPRINT",EDGE,{"derivedFrom":subQ0}),1.0]])]});}
            var Q45;
            {var subQ0=sQuery(id+"F2.wireOp",EDGE,"E16.3.44.0");Q45=makeQuery(id+"F2.imprint","IMPRINT",FACE,{"disambiguationData":[TD([[makeQuery(id+"F2.imprint","IMPRINT",EDGE,{"derivedFrom":subQ0}),1.0]])]});}
            var Q46;
            {var subQ0=sQuery(id+"F2.wireOp",EDGE,"E16.3.45.0");Q46=makeQuery(id+"F2.imprint","IMPRINT",FACE,{"disambiguationData":[TD([[makeQuery(id+"F2.imprint","IMPRINT",EDGE,{"derivedFrom":subQ0}),1.0]])]});}
            var Q47;
            {var subQ0=sQuery(id+"F2.wireOp",EDGE,"E16.3.46.0");Q47=makeQuery(id+"F2.imprint","IMPRINT",FACE,{"disambiguationData":[TD([[makeQuery(id+"F2.imprint","IMPRINT",EDGE,{"derivedFrom":subQ0}),1.0]])]});}
            var Q48;
            {var subQ0=sQuery(id+"F2.wireOp",EDGE,"E16.3.47.0");Q48=makeQuery(id+"F2.imprint","IMPRINT",FACE,{"disambiguationData":[TD([[makeQuery(id+"F2.imprint","IMPRINT",EDGE,{"derivedFrom":subQ0}),1.0]])]});}
            var Q49;
            {var subQ0=sQuery(id+"F2.wireOp",EDGE,"E16.3.48.0");Q49=makeQuery(id+"F2.imprint","IMPRINT",FACE,{"disambiguationData":[TD([[makeQuery(id+"F2.imprint","IMPRINT",EDGE,{"derivedFrom":subQ0}),1.0]])]});}
            var Q50;
            {var subQ0=sQuery(id+"F2.wireOp",EDGE,"E16.3.49.0");Q50=makeQuery(id+"F2.imprint","IMPRINT",FACE,{"disambiguationData":[TD([[makeQuery(id+"F2.imprint","IMPRINT",EDGE,{"derivedFrom":subQ0}),1.0]])]});}
            var Q51;
            Q51=makeQuery(id+"F1.opExtrude","SWEPT_FACE",FACE,{"disambiguationData":[OSD([sQuery(id+"F0.wireOp",EDGE,"E2")])]});
            extrude(context, id + "F3", {"entities" : qUnion([Q0, Q1, Q2, Q3, Q4, Q5, Q6, Q7, Q8, Q9, Q10, Q11, Q12, Q13, Q14, Q15, Q16, Q17, Q18, Q19, Q20, Q21, Q22, Q23, Q24, Q25, Q26, Q27, Q28, Q29, Q30, Q31, Q32, Q33, Q34, Q35, Q36, Q37, Q38, Q39, Q40, Q41, Q42, Q43, Q44, Q45, Q46, Q47, Q48, Q49, Q50]), "operationType" : NewBodyOperationType.ADD, "endBound" : BoundingType.UP_TO_SURFACE, "oppositeDirection" : true, "endBoundEntityFace" : qUnion([Q51]), "depth" : 25.4 * mm});
        }
        {
            var Q0;
            Q0=makeQuery(id+"F1.opExtrude","CAP_FACE",FACE,{"disambiguationData":[OSD([sQuery(id+"F0.wireOp",EDGE,"E0"),sQuery(id+"F0.wireOp",EDGE,"E1"),sQuery(id+"F0.wireOp",EDGE,"E2"),sQuery(id+"F0.wireOp",EDGE,"E3")])],"isStart":true});
            var sketch = newSketch(context, id + "F4", { "sketchPlane" : qUnion([Q0])});
            skLineSegment(sketch, "E20", {"start": v(-378.33, -144.66) * mm, "end": v(-378.33, -106.56) * mm});
            skLineSegment(sketch, "E21", {"start": v(-365.63, -93.86) * mm, "end": v(-340.23, -93.86) * mm});
            skLineSegment(sketch, "E22", {"start": v(-327.53, -106.56) * mm, "end": v(-327.53, -144.66) * mm});
            skPoint(sketch, "E23.visualSharp", {"position": v(-327.53, -93.86) * mm});
            skArc(sketch, "E23.filletArc", {"start": v(-327.53, -106.56) * mm, "mid": v(-331.25, -97.58) * mm, "end": v(-340.23, -93.86) * mm});
            skPoint(sketch, "E24.visualSharp", {"position": v(-378.33, -93.86) * mm});
            skArc(sketch, "E24.filletArc", {"start": v(-365.63, -93.86) * mm, "mid": v(-374.61, -97.58) * mm, "end": v(-378.33, -106.56) * mm});
            skLineSegment(sketch, "E25", {"start": v(383.67, -144.66) * mm, "end": v(383.67, -106.56) * mm});
            skLineSegment(sketch, "E26", {"start": v(370.97, -93.86) * mm, "end": v(345.57, -93.86) * mm});
            skLineSegment(sketch, "E27", {"start": v(332.87, -106.56) * mm, "end": v(332.87, -144.66) * mm});
            skLineSegment(sketch, "E28", {"start": v(332.87, -144.66) * mm, "end": v(383.67, -144.66) * mm});
            skPoint(sketch, "E29.visualSharp", {"position": v(332.87, -93.86) * mm});
            skArc(sketch, "E29.filletArc", {"start": v(345.57, -93.86) * mm, "mid": v(336.59, -97.58) * mm, "end": v(332.87, -106.56) * mm});
            skPoint(sketch, "E30.visualSharp", {"position": v(383.67, -93.86) * mm});
            skArc(sketch, "E30.filletArc", {"start": v(383.67, -106.56) * mm, "mid": v(379.95, -97.58) * mm, "end": v(370.97, -93.86) * mm});
            skLineSegment(sketch, "E31", {"start": v(-378.33, -208.16) * mm, "end": v(383.67, -208.16) * mm, "construction": true});
            skLineSegment(sketch, "E32.MirrorCS", {"start": v(-378.33, -271.66) * mm, "end": v(-378.33, -309.76) * mm});
            skLineSegment(sketch, "E33.MirrorCS", {"start": v(-327.53, -309.76) * mm, "end": v(-327.53, -271.66) * mm});
            skArc(sketch, "E34.MirrorCS", {"start": v(-365.63, -322.46) * mm, "mid": v(-374.61, -318.74) * mm, "end": v(-378.33, -309.76) * mm});
            skLineSegment(sketch, "E35.MirrorCS", {"start": v(-365.63, -322.46) * mm, "end": v(-340.23, -322.46) * mm});
            skArc(sketch, "E36.MirrorCS", {"start": v(-327.53, -309.76) * mm, "mid": v(-331.25, -318.74) * mm, "end": v(-340.23, -322.46) * mm});
            skLineSegment(sketch, "E37.MirrorCS", {"start": v(383.67, -271.66) * mm, "end": v(383.67, -309.76) * mm});
            skArc(sketch, "E38.MirrorCS", {"start": v(383.67, -309.76) * mm, "mid": v(379.95, -318.74) * mm, "end": v(370.97, -322.46) * mm});
            skLineSegment(sketch, "E39.MirrorCS", {"start": v(370.97, -322.46) * mm, "end": v(345.57, -322.46) * mm});
            skArc(sketch, "E40.MirrorCS", {"start": v(345.57, -322.46) * mm, "mid": v(336.59, -318.74) * mm, "end": v(332.87, -309.76) * mm});
            skLineSegment(sketch, "E41.MirrorCS", {"start": v(332.87, -309.76) * mm, "end": v(332.87, -271.66) * mm});
            skSolve(sketch);
        }
        {
            var Q0;
            {var subQ1=sQuery(id+"F4.wireOp",EDGE,"E20");Q0=makeQuery(id+"F4.imprint","IMPRINT",FACE,{"disambiguationData":[TD([[makeQuery(id+"F4.imprint","IMPRINT",EDGE,{"derivedFrom":subQ1}),-1.0]])]});}
            var Q1;
            {var subQ0=sQuery(id+"F4.wireOp",EDGE,"E32.MirrorCS");Q1=makeQuery(id+"F4.imprint","IMPRINT",FACE,{"disambiguationData":[TD([[makeQuery(id+"F4.imprint","IMPRINT",EDGE,{"derivedFrom":subQ0}),1.0]])]});}
            var Q2;
            {var subQ0=sQuery(id+"F4.wireOp",EDGE,"E37.MirrorCS");Q2=makeQuery(id+"F4.imprint","IMPRINT",FACE,{"disambiguationData":[TD([[makeQuery(id+"F4.imprint","IMPRINT",EDGE,{"derivedFrom":subQ0}),-1.0]])]});}
            var Q3;
            Q3=makeQuery(id+"F4.imprint","IMPRINT",FACE,{"disambiguationData":[TD([[makeQuery(id+"F4.imprint","IMPRINT",EDGE,{"derivedFrom":sQuery(id+"F4.wireOp",EDGE,"E25")}),1.0]])]});
            extrude(context, id + "F5", {"entities" : qUnion([Q0, Q1, Q2, Q3]), "operationType" : NewBodyOperationType.ADD, "oppositeDirection" : true, "depth" : 12.7 * mm});
        }
        {
            var Q0;
            Q0=makeQuery(id+"F5.opExtrude","CAP_FACE",FACE,{"disambiguationData":[OSD([sQuery(id+"F4.wireOp",EDGE,"E25"),sQuery(id+"F4.wireOp",EDGE,"E26"),sQuery(id+"F4.wireOp",EDGE,"E27"),sQuery(id+"F4.wireOp",EDGE,"E28"),sQuery(id+"F4.wireOp",EDGE,"E29.filletArc"),sQuery(id+"F4.wireOp",EDGE,"E30.filletArc")])],"isStart":false});
            var sketch = newSketch(context, id + "F6", { "sketchPlane" : qUnion([Q0])});
            skPoint(sketch, "E42", {"position": v(-370.97, -119.26) * mm});
            skPoint(sketch, "E43", {"position": v(-345.57, -119.26) * mm});
            skSolve(sketch);
        }
        {
            var Q0;
            Q0=makeQuery(id+"F5.opExtrude","CAP_FACE",FACE,{"disambiguationData":[OSD([sQuery(id+"F0.wireOp",EDGE,"E0"),sQuery(id+"F4.wireOp",EDGE,"E37.MirrorCS"),sQuery(id+"F4.wireOp",EDGE,"E38.MirrorCS"),sQuery(id+"F4.wireOp",EDGE,"E39.MirrorCS"),sQuery(id+"F4.wireOp",EDGE,"E40.MirrorCS"),sQuery(id+"F4.wireOp",EDGE,"E41.MirrorCS")])],"isStart":false});
            var sketch = newSketch(context, id + "F7", { "sketchPlane" : qUnion([Q0])});
            skPoint(sketch, "E44", {"position": v(-370.97, -297.06) * mm});
            skPoint(sketch, "E45", {"position": v(-345.57, -297.06) * mm});
            skSolve(sketch);
        }
        {
            var Q0;
            Q0=makeQuery(id+"F5.opExtrude","CAP_FACE",FACE,{"disambiguationData":[OSD([sQuery(id+"F0.wireOp",EDGE,"E2"),sQuery(id+"F4.wireOp",EDGE,"E20"),sQuery(id+"F4.wireOp",EDGE,"E21"),sQuery(id+"F4.wireOp",EDGE,"E22"),sQuery(id+"F4.wireOp",EDGE,"E23.filletArc"),sQuery(id+"F4.wireOp",EDGE,"E24.filletArc")])],"isStart":false});
            var sketch = newSketch(context, id + "F8", { "sketchPlane" : qUnion([Q0])});
            skPoint(sketch, "E46", {"position": v(340.23, -119.26) * mm});
            skPoint(sketch, "E47", {"position": v(365.63, -119.26) * mm});
            skSolve(sketch);
        }
        {
            var Q0;
            Q0=makeQuery(id+"F5.opExtrude","CAP_FACE",FACE,{"disambiguationData":[OSD([sQuery(id+"F0.wireOp",EDGE,"E0"),sQuery(id+"F4.wireOp",EDGE,"E32.MirrorCS"),sQuery(id+"F4.wireOp",EDGE,"E33.MirrorCS"),sQuery(id+"F4.wireOp",EDGE,"E34.MirrorCS"),sQuery(id+"F4.wireOp",EDGE,"E35.MirrorCS"),sQuery(id+"F4.wireOp",EDGE,"E36.MirrorCS")])],"isStart":false});
            var sketch = newSketch(context, id + "F9", { "sketchPlane" : qUnion([Q0])});
            skPoint(sketch, "E48", {"position": v(340.23, -297.06) * mm});
            skPoint(sketch, "E49", {"position": v(365.63, -297.06) * mm});
            skSolve(sketch);
        }
        {
            var Q0;
            Q0=sQuery(id+"F6.wireOp",VERTEX,"E42");
            var Q1;
            Q1=sQuery(id+"F6.wireOp",VERTEX,"E43");
            var Q2;
            Q2=sQuery(id+"F7.wireOp",VERTEX,"E44");
            var Q3;
            Q3=sQuery(id+"F7.wireOp",VERTEX,"E45");
            var Q4;
            Q4=sQuery(id+"F9.wireOp",VERTEX,"E48");
            var Q5;
            Q5=sQuery(id+"F9.wireOp",VERTEX,"E49");
            var Q6;
            Q6=sQuery(id+"F8.wireOp",VERTEX,"E46");
            var Q7;
            Q7=sQuery(id+"F8.wireOp",VERTEX,"E47");
            var Q8;
            Q8=makeQuery(id+"F1.opExtrude","SWEPT_BODY",BODY,{"disambiguationData":[OSD([sQuery(id+"F0.wireOp",EDGE,"E0"),sQuery(id+"F0.wireOp",EDGE,"E1"),sQuery(id+"F0.wireOp",EDGE,"E2"),sQuery(id+"F0.wireOp",EDGE,"E3")])]});
            hole(context, id + "F10", {"style" : HoleStyle.C_BORE, "endStyle" : HoleEndStyle.THROUGH, "holeDiameter" : 6.35 * mm, "cBoreDiameter" : 12.7 * mm, "cBoreDepth" : 3.17 * mm, "tappedDepth" : 12.7 * mm, "tapClearance" : 3, "locations" : qUnion([Q0, Q1, Q2, Q3, Q4, Q5, Q6, Q7]), "scope" : qUnion([Q8])});
        }
    });
